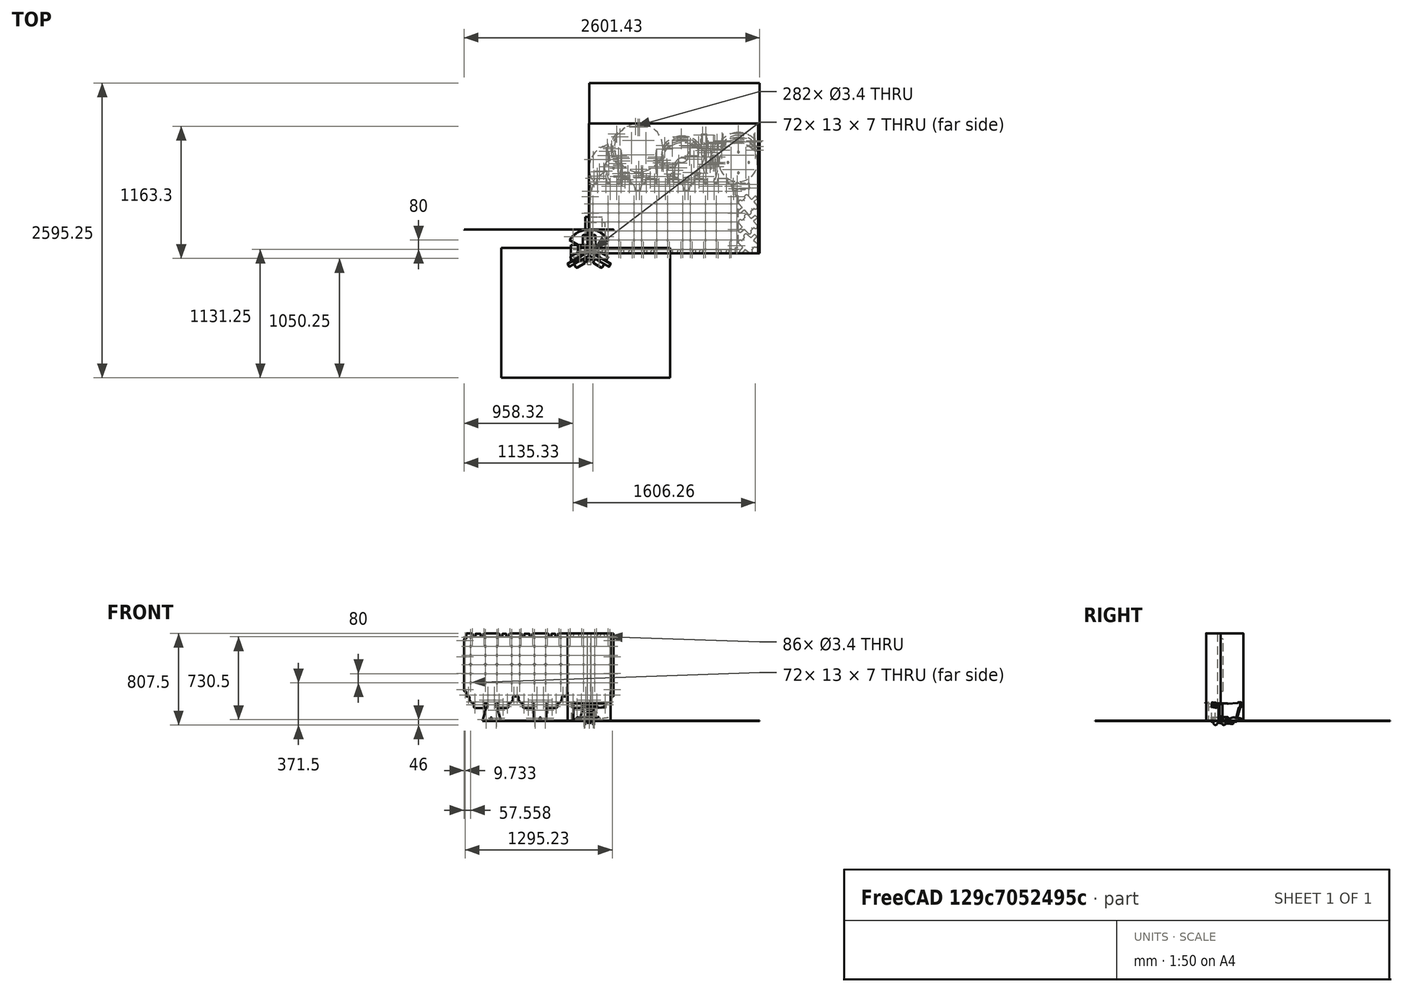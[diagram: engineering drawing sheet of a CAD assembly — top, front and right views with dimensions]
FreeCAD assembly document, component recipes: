
FREECAD ASSEMBLY — COMPONENT RECIPES ("composit_stand_small_3")

This assembly document has 19 components, labeled P0..P18 below (a component is one placed body or linked part). 18 of them carry a construction recipe — the FreeCAD feature program that regenerates the part from scratch, quoted from this document or its linked companion documents; the rest are supplied as boundary geometry only. No exploded tour is included for this assembly.
NOTE — this tour is split across 2 documents so each fits a 32k-token context. This is document 1: the component sections continue in the remaining 1 document, each repeating the header above.
COMPONENT P0 — recipe-attached ("gutter001_material_0.50ansi", modeled in this document).
Construction recipe (the document's own serialized feature program — sketch geometry with constraints, then the solid features built on it; lengths are millimeters unless a unit is written):

FEATURE [Sketcher::SketchObject] Sketch  label="gutter_side_sketch"
  FullyConstrained = true
  MapMode = 5
  Support = -> [XY_Plane]
  expr: .AttachmentOffset.Base.x = 0
  expr: .Constraints.little_distance = <<gutter>>.low_edge_length + (<<main>>.inner_width - <<main>>.thickness * 2) / 2 - 3mm
  expr: Constraints[12] = <<gutter>>.length
  expr: Constraints[27] = <<gutter>>.bend_angle + 90°
  sketch-geometry (15):
    g0: LineSegment StartX=0 StartY=150 StartZ=0 EndX=13.5 EndY=150 EndZ=0
    g1: LineSegment StartX=27 StartY=0 StartZ=0 EndX=0 EndY=0 EndZ=0
    g2: LineSegment StartX=15 StartY=148.5 StartZ=0 EndX=15 EndY=120 EndZ=0
    g3: LineSegment StartX=15 StartY=120 StartZ=0 EndX=31.2589 EndY=120 EndZ=0
    g4: GeomPoint X=27 Y=150 Z=0
    g5: ArcOfCircle CenterX=31.2589 CenterY=116.5 CenterZ=0 NormalX=0 NormalY=0 NormalZ=1 AngleXU=0 Radius=3.5 StartAngle=6.21662 EndAngle=7.85398
    g6: GeomPoint X=27 Y=0 Z=0
    g7: ArcOfCircle CenterX=13.5 CenterY=148.5 CenterZ=0 NormalX=0 NormalY=0 NormalZ=1 AngleXU=0 Radius=1.5 StartAngle=-3.6e-15 EndAngle=1.5708
    g8: GeomPoint X=15 Y=150 Z=0
    g9: LineSegment StartX=34.7511 StartY=116.267 StartZ=0 EndX=27.4178 EndY=6.26718 EndZ=0
    g10: LineSegment StartX=27.4178 StartY=6.26718 StartZ=0 EndX=27 EndY=0 EndZ=0
    g11: ArcOfCircle CenterX=23.9256 CenterY=6.5 CenterZ=0 NormalX=0 NormalY=0 NormalZ=1 AngleXU=0 Radius=3.5 StartAngle=4.71239 EndAngle=6.21662
    g12: LineSegment StartX=0 StartY=0 StartZ=0 EndX=0 EndY=3 EndZ=0
    g13: LineSegment StartX=0 StartY=3 StartZ=0 EndX=0 EndY=150 EndZ=0
    g14: LineSegment StartX=0 StartY=3 StartZ=0 EndX=23.9256 EndY=3 EndZ=0
  constraints (36):
    c: Coincident(g-1,g12)
    c: PointOnObject(g13,g-2)
    c: Coincident(g13,g0)
    c: Horizontal(g0)
    c: PointOnObject(g6,g-1)
    c: Coincident(g1,g12)
    c: Distance(g1,g6) = 27  'little_distance'
    c: Vertical(g2)
    c: Coincident(g3,g2)
    c: Horizontal(g3)
    c: DistanceY(g2,g8) = 30
    c: PointOnObject(g4,g0)
    c: Distance(g6,g4) = 150
    c: Distance(g0,g8) = 15
    c: Tangent(g3,g5) = 1.5708
    c: Diameter(g5) = 7
    c: PointOnObject(g8,g0)
    c: PointOnObject(g8,g2)
    c: Tangent(g0,g7) = 1.5708
    c: Tangent(g2,g7) = 1.5708
    c: Diameter(g7) = 3
    c: Tangent(g9,g5) = 1.5708
    c: Vertical(g4,g6)
    c: Coincident(g1,g6)
    c: Coincident(g10,g1)
    c: Coincident(g9,g10)
    c: Parallel(g9,g10)
    c: Angle(g10,g-1) = 1.63736
    c: Coincident(g12,g13)
    c: Vertical(g12)
    c: Coincident(g14,g12)
    c: Horizontal(g14)
    c: Tangent(g11,g9) = 1.5708
    c: Tangent(g14,g11) = -1.5708
    c: Equal(g11,g5)
    c: DistanceY(g12,g12) = 3
FEATURE [PartDesign::Pad] Pad  label="gutter_side_pad"
  Direction = (0,0,1)
  Length = 0.3
  Length2 = 10
  Profile = -> Sketch
  ReferenceAxis = -> Sketch [N_Axis]
  Type = 0
FEATURE [Sketcher::SketchObject] Sketch010
  FullyConstrained = true
  MapMode = 5
  Support = -> [XY_Plane]
  expr: Constraints[2] = -(<<main>>.inner_width / 2 - <<main>>.thickness - <<main>>.bend_r)
  expr: Constraints[3] = <<gutter>>.length
  sketch-geometry (1):
    g0: LineSegment StartX=-9.99 StartY=0 StartZ=0 EndX=-9.99 EndY=150 EndZ=0
  constraints (4):
    c: PointOnObject(g0,g-1)
    c: Vertical(g0)
    c: DistanceX(g0) = -9.99
    c: DistanceY(g0) = 150
FEATURE [PartDesign::Mirrored] Mirrored005
  BaseFeature = -> Pad
  MirrorPlane = -> YZ_Plane
  Originals = -> [Pad]
  Refine = true
FEATURE [PartDesign::CoordinateSystem] Local_CS001
  AttacherType = Attacher::AttachEngine3D
  AttachmentOffset = pos=(-30,0,0) rot=(0,0,1;0.066568rad)
  MapMode = 5
  Placement = pos=(-30,0,0) rot=(0,0,1;0.066568rad)
  Support = -> [XY_Plane]
  expr: .AttachmentOffset.Base.x = -(<<gutter>>.low_edge_length + (<<main>>.inner_width - <<main>>.thickness * 2) / 2)
  expr: .AttachmentOffset.Rotation.Angle = <<gutter>>.bend_angle
  expr: .AttachmentOffset.Rotation.Yaw = <<gutter>>.bend_angle
FEATURE [PartDesign::CoordinateSystem] Local_CS002
  AttacherType = Attacher::AttachEngine3D
  AttachmentOffset = pos=(30,0,0) rot=(0,0,1;-0.066568rad)
  MapMode = 5
  Placement = pos=(30,0,0) rot=(0,0,1;6.21662rad)
  Support = -> [XY_Plane]
  expr: .AttachmentOffset.Base.x = <<gutter>>.low_edge_length + (<<main>>.inner_width - <<main>>.thickness * 2) / 2
  expr: .AttachmentOffset.Rotation.Angle = -<<gutter>>.bend_angle
FEATURE [PartDesign::CoordinateSystem] Local_CS003
  AttacherType = Attacher::AttachEngine3D
  AttachmentOffset = pos=(0,60,0) rot=(0,0,1;1.5708rad)
  MapMode = 5
  Placement = pos=(33.9911,59.8671,0) rot=(0,0,1;1.50423rad)
  Support = -> [Local_CS002]
  expr: .AttachmentOffset.Base.y = <<gutter>>.plane_middle
FEATURE [PartDesign::CoordinateSystem] Local_CS004
  AttacherType = Attacher::AttachEngine3D
  AttachmentOffset = pos=(2,60,0) rot=(0,0,1;-1.5708rad)
  MapMode = 5
  Placement = pos=(-31.9956,60.0001,0) rot=(0,0,1;4.77896rad)
  Support = -> [Local_CS001]
  expr: .AttachmentOffset.Base.y = <<gutter>>.plane_middle
FEATURE [PartDesign::Plane] DatumPlane003
  Length = 91.4351
  MapMode = 4
  Placement = pos=(33.9911,59.8671,0) rot=(0.023538,0.706911,0.706911;3.09453rad)
  ResizeMode = 0
  Support = -> [Local_CS003]
  Width = 62.5599
FEATURE [PartDesign::Plane] DatumPlane004
  Length = 91.4351
  MapMode = 4
  Placement = pos=(-31.9956,60.0001,0) rot=(0.998893,0.03326,0.03326;1.5719rad)
  ResizeMode = 0
  Support = -> [Local_CS004]
  Width = 62.5599
FEATURE [PartDesign::Plane] DatumPlane005
  AttachmentOffset = pos=(0,-1,0) rot=(0,0,1;0rad)
  Length = 202.865
  MapMode = 5
  Placement = pos=(34.9889,59.8006,0) rot=(0,0,1;1.50423rad)
  ResizeMode = 0
  Support = -> [Local_CS003]
  Width = 102.646
FEATURE [PartDesign::Plane] DatumPlane006
  Length = 202.865
  MapMode = 5
  Placement = pos=(-31.9956,60.0001,0) rot=(0,0,-1;1.50423rad)
  ResizeMode = 0
  Support = -> [Local_CS004]
  Width = 102.646
FEATURE [Sketcher::SketchObject] Sketch037
  AttachmentOffset = pos=(30,2,0) rot=(0,0,1;0rad)
  FullyConstrained = true
  MapMode = 5
  Placement = pos=(33.9911,89.9337,0) rot=(0,0,1;1.50423rad)
  Support = -> [Local_CS003]
  expr: .AttachmentOffset.Base.x = <<dropper>>.distance_between_droppers1 / 2
  expr: Constraints[10] = <<dropper>>.d
  sketch-geometry (8):
    g0: LineSegment StartX=0 StartY=11.625 StartZ=0 EndX=1 EndY=11.625 EndZ=0
    g1: ArcOfCircle CenterX=1 CenterY=0 CenterZ=0 NormalX=0 NormalY=0 NormalZ=1 AngleXU=0 Radius=11.625 StartAngle=0.450911 EndAngle=1.5708
    g2: ArcOfCircle CenterX=17.127 CenterY=0 CenterZ=0 NormalX=0 NormalY=0 NormalZ=1 AngleXU=0 Radius=3 StartAngle=0.25268 EndAngle=1.29556
    g3: LineSegment StartX=12.0914 StartY=4.53943 StartZ=0 EndX=17.9423 EndY=2.88708 EndZ=0
    g4: LineSegment StartX=0 StartY=11.625 StartZ=0 EndX=0 EndY=0 EndZ=0
    g5: LineSegment StartX=0 StartY=0 StartZ=0 EndX=21 EndY=0 EndZ=0
    g6: ArcOfCircle CenterX=21 CenterY=1 CenterZ=0 NormalX=0 NormalY=0 NormalZ=1 AngleXU=0 Radius=1 StartAngle=3.39427 EndAngle=4.71239
    g7: ArcOfCircle CenterX=12.3631 CenterY=5.5018 CenterZ=0 NormalX=0 NormalY=0 NormalZ=1 AngleXU=0 Radius=1 StartAngle=3.5925 EndAngle=4.43715
  constraints (22):
    c: PointOnObject(g0,g-2)
    c: Horizontal(g0)
    c: PointOnObject(g2,g-1)
    c: Tangent(g3,g2) = 1.5708
    c: Tangent(g1,g0) = 1.5708
    c: Coincident(g4,g0)
    c: Coincident(g4,g-1)
    c: Coincident(g5,g4)
    c: Diameter(g2) = 6
    c: Angle(g3,g-1) = 0.275238
    c: Diameter(g1) = 23.25
    c: PointOnObject(g1,g-1)
    c: Distance(g0) = 1
    c: Horizontal(g5)
    c: Tangent(g6,g5) = -1.5708
    c: Tangent(g6,g2) = 1.5708
    c: Diameter(g6) = 2
    c: Distance(g5) = 21
    c: Tangent(g3,g7) = -1.5708
    c: Tangent(g1,g7) = 1.5708
    c: Diameter(g7) = 2
    c: DistanceY(g2) = 2.88708  'arc_height'
FEATURE [PartDesign::Pocket] Pocket008
  BaseFeature = -> Mirrored005
  Direction = (0,0,-1)
  Length = 5
  Length2 = 5
  Midplane = true
  Profile = -> Sketch037
  ReferenceAxis = -> Sketch037 [N_Axis]
  Type = 1
FEATURE [PartDesign::Mirrored] Mirrored006
  MirrorPlane = -> Sketch037 [V_Axis]
FEATURE [PartDesign::Mirrored] Mirrored007
  MirrorPlane = -> DatumPlane003
FEATURE [PartDesign::MultiTransform] MultiTransform002
  BaseFeature = -> Pocket008
  Originals = -> [Pocket008]
  Transformations = -> [Mirrored006,Mirrored007]
FEATURE [PartDesign::SubShapeBinder] Binder
  AttacherType = Attacher::AttachEngine3D
  AttachmentOffset = pos=(35,0,0) rot=(0,0,1;0rad)
  BindCopyOnChange = 0
  BindMode = 0
  ClaimChildren = true
  Context = -> Body [Binder.]
  Fuse = false
  MakeFace = true
  MapMode = 5
  OffsetFill = false
  OffsetIntersection = false
  OffsetJoinType = 0
  OffsetOpenResult = false
  PartialLoad = false
  Placement = pos=(-28.1674,25.0777,0) rot=(0,0,-1;1.50423rad)
  Relative = false
  _Version = 2
  expr: .AttachmentOffset.Base.x = <<dropper>>.distance_between_droppers2 / 2
FEATURE [PartDesign::Pocket] Pocket009
  BaseFeature = -> MultiTransform002
  Direction = (0,0,-1)
  Length = 5
  Length2 = 5
  Midplane = true
  Profile = -> Binder
  Type = 1
FEATURE [PartDesign::Plane] DatumPlane007
  Length = 91.4351
  MapMode = 4
  Placement = pos=(-28.1674,25.0777,0) rot=(0.998893,0.03326,0.03326;1.5719rad)
  ResizeMode = 0
  Support = -> [Binder]
  Width = 62.5599
FEATURE [PartDesign::Mirrored] Mirrored008
  MirrorPlane = -> DatumPlane007
FEATURE [PartDesign::Mirrored] Mirrored009
  MirrorPlane = -> DatumPlane004
FEATURE [PartDesign::MultiTransform] MultiTransform003
  BaseFeature = -> Pocket009
  Originals = -> [Pocket009]
  Transformations = -> [Mirrored008,Mirrored009]
FEATURE [Sketcher::SketchObject] Sketch038
  FullyConstrained = true
  MapMode = 5
  Support = -> [XY_Plane]
  expr: Constraints[2] = <<main>>.inner_width / 2 - <<main>>.thickness - <<main>>.bend_r
  expr: Constraints[3] = <<gutter>>.length
  sketch-geometry (1):
    g0: LineSegment StartX=9.99 StartY=0 StartZ=0 EndX=9.99 EndY=150 EndZ=0
  constraints (4):
    c: PointOnObject(g0,g-1)
    c: Vertical(g0)
    c: DistanceX(g0) = 9.99
    c: DistanceY(g0) = 150
FEATURE [Sketcher::SketchObject] Sketch039
  AttachmentOffset = pos=(51,14,0) rot=(0,0,1;0rad)
  FullyConstrained = true
  MapMode = 5
  Placement = pos=(24.4124,111.619,0) rot=(0,0,1;1.50423rad)
  Support = -> [DatumPlane005]
  expr: .AttachmentOffset.Base.x = <<main>>.gutter_fix_holes_distance
  expr: Constraints[1] = <<main>>.rivet_d
  sketch-geometry (1):
    g0: Circle CenterX=0 CenterY=0 CenterZ=0 NormalX=0 NormalY=0 NormalZ=1 AngleXU=0 Radius=1.7
  constraints (2):
    c: Coincident(g0,g-1)
    c: Diameter(g0) = 3.4
FEATURE [PartDesign::Pocket] Pocket010
  BaseFeature = -> MultiTransform003
  Direction = (0,0,-1)
  Length = 5
  Length2 = 5
  Midplane = true
  Profile = -> Sketch039
  ReferenceAxis = -> Sketch039 [N_Axis]
  Type = 1
FEATURE [PartDesign::Mirrored] Mirrored010
  MirrorPlane = -> DatumPlane003
FEATURE [PartDesign::Mirrored] Mirrored011
  MirrorPlane = -> YZ_Plane
FEATURE [PartDesign::MultiTransform] MultiTransform004
  BaseFeature = -> Pocket010
  Originals = -> [Pocket010]
  Transformations = -> [Mirrored010,Mirrored011]
FEATURE [PartDesign::FeaturePython] Fold  # WARN: FeaturePython — macro-defined, semantics opaque (R4)
  BaseFeature = -> MultiTransform004
  BendLine = -> Sketch038
  Position = 0
  angle = 90
  baseObject = -> MultiTransform004 [Face4]
  invert = false
  invertbend = true
  kfactor = 0.01
  radius = 0.01
  unfold = false
  expr: radius = <<main>>.bend_r
FEATURE [PartDesign::FeaturePython] Fold002  # WARN: FeaturePython — macro-defined, semantics opaque (R4)
  BaseFeature = -> Fold
  BendLine = -> Sketch010
  Position = 0
  angle = 90
  baseObject = -> Fold [Face2]
  invert = false
  invertbend = false
  kfactor = 0.01
  radius = 0.01
  unfold = false
  expr: radius = <<main>>.bend_r
FEATURE [PartDesign::CoordinateSystem] Local_CS024
  AttacherType = Attacher::AttachEngine3D
  AttachmentOffset = pos=(0,60,-10.3215) rot=(-1,0,0;0.066568rad)
  MapMode = 5
  Placement = pos=(0,60,-10.3215) rot=(-1,0,0;0.066568rad)
  Support = -> [XY_Plane]
  expr: .AttachmentOffset.Base.y = <<gutter>>.plane_middle
  expr: .AttachmentOffset.Base.z = (-6.929mm - 13.714mm) / 2
  expr: .AttachmentOffset.Rotation.Roll = -<<gutter>>.bend_angle
FEATURE [Sketcher::SketchObject] Sketch115
  FullyConstrained = true
  MapMode = 5
  Support = -> [XY_Plane]
  expr: Constraints[1] = <<main>>.rivet_d
  sketch-geometry (1):
    g0: Circle CenterX=0 CenterY=145 CenterZ=0 NormalX=0 NormalY=0 NormalZ=1 AngleXU=0 Radius=1.7
  constraints (3):
    c: PointOnObject(g0,g-2)
    c: Diameter(g0) = 3.4
    c: DistanceY(g0) = 145
FEATURE [PartDesign::Pocket] Pocket070
  BaseFeature = -> Fold002
  Direction = (0,0,-1)
  Length = 5
  Length2 = 5
  Midplane = true
  Profile = -> Sketch115
  ReferenceAxis = -> Sketch115 [N_Axis]
  Type = 1
FEATURE [PartDesign::Body] Body  label="gutter001_material_0.50ansi"
  Group = -> [Sketch,Pad,Mirrored005,Local_CS001,Local_CS002,Local_CS003,Local_CS004,DatumPlane003,DatumPlane004,DatumPlane005,DatumPlane006,Sketch037,Pocket008,MultiTransform002,Mirrored006,Mirrored007,Binder,Pocket009,MultiTransform003,Mirrored008,DatumPlane007,Mirrored009,Sketch010,Sketch038,Sketch039,Pocket010,MultiTransform004,Mirrored010,Mirrored011,Fold,Fold002,Local_CS024,Sketch115,Pocket070]
  Origin = -> Origin
  Tip = -> Pocket070
COMPONENT P1 — recipe-attached ("Body001_material_0.30ansi", modeled in this document).
Construction recipe (the document's own serialized feature program — sketch geometry with constraints, then the solid features built on it; lengths are millimeters unless a unit is written):

FEATURE [Sketcher::SketchObject] Sketch003  label="main_sketch"
  FullyConstrained = true
  MapMode = 5
  Support = -> [XY_Plane001]
  expr: Constraints[30] = <<main>>.end_face_width
  expr: Constraints[31] = <<main>>.work_plane_width
  expr: Constraints[44] = <<main>>.al_thickness
  sketch-geometry (17):
    g0: LineSegment StartX=-16 StartY=9.2376 StartZ=0 EndX=-16 EndY=209.238 EndZ=0
    g1: LineSegment StartX=-16 StartY=209.238 StartZ=0 EndX=16 EndY=209.238 EndZ=0
    g2: LineSegment StartX=16 StartY=209.238 StartZ=0 EndX=16 EndY=9.2376 EndZ=0
    g3: LineSegment StartX=16 StartY=9.2376 StartZ=0 EndX=189.205 EndY=-90.7624 EndZ=0
    g4: LineSegment StartX=189.205 StartY=-90.7624 StartZ=0 EndX=173.205 EndY=-118.475 EndZ=0
    g5: LineSegment StartX=173.205 StartY=-118.475 StartZ=0 EndX=0 EndY=-18.4752 EndZ=0
    g6: LineSegment StartX=0 StartY=-18.4752 StartZ=0 EndX=-173.205 EndY=-118.475 EndZ=0
    g7: LineSegment StartX=-173.205 StartY=-118.475 StartZ=0 EndX=-189.205 EndY=-90.7624 EndZ=0
    g8: LineSegment StartX=-189.205 StartY=-90.7624 StartZ=0 EndX=-16 EndY=9.2376 EndZ=0
    g9: LineSegment StartX=-16 StartY=9.2376 StartZ=0 EndX=0 EndY=0 EndZ=0
    g10: LineSegment StartX=0 StartY=0 StartZ=0 EndX=16 EndY=9.2376 EndZ=0
    g11: LineSegment StartX=0 StartY=0 StartZ=0 EndX=0 EndY=-18.4752 EndZ=0
    g12: LineSegment StartX=189.205 StartY=-90.7624 StartZ=0 EndX=13 EndY=10.9697 EndZ=0
    g13: LineSegment StartX=16 StartY=209.238 StartZ=0 EndX=16 EndY=9.42236 EndZ=0
    g14: LineSegment StartX=16 StartY=9.42236 StartZ=0 EndX=15.7 EndY=9.42236 EndZ=0
    g15: LineSegment StartX=13 StartY=10.9697 StartZ=0 EndX=13 EndY=30.9697 EndZ=0
    g16: LineSegment StartX=13 StartY=10.9697 StartZ=0 EndX=6.66667 EndY=0 EndZ=0
  constraints (56):
    c: Vertical(g0)
    c: Coincident(g0,g1)
    c: Horizontal(g1)
    c: Coincident(g1,g2)
    c: Vertical(g2)
    c: Coincident(g2,g3)
    c: Coincident(g3,g4)
    c: Coincident(g4,g5)
    c: PointOnObject(g5,g-2)
    c: Coincident(g5,g6)
    c: Coincident(g6,g7)
    c: Coincident(g8,g7)
    c: Equal(g2,g6)
    c: Equal(g6,g5)
    c: Equal(g5,g3)
    c: Equal(g4,g7)
    c: Equal(g7,g1)
    c: Perpendicular(g4,g5)
    c: Perpendicular(g4,g3)
    c: Perpendicular(g7,g6)
    c: Perpendicular(g8,g7)
    c: Angle(g6,g5) = 2.0944
    c: Angle(g3,g2) = 2.0944
    c: Coincident(g9,g0)
    c: Coincident(g9,g-1)
    c: Coincident(g10,g9)
    c: Coincident(g10,g2)
    c: Coincident(g11,g9)
    c: Coincident(g11,g5)
    c: Equal(g10,g11)
    c: DistanceX(g1,g1) = 32
    c: DistanceY(g2,g2) = 200
    c: DistanceY(g9,g2) = 9.2376  'petal_offset'
    c: DistanceY(g0) = 9.2376  'petal_conn_y'
    c: Coincident(g8,g0)
    c: DistanceX(g2) = 16  'petal_conn_x'
    c: Distance(g9,g1) = 209.848  'max_r'
    c: Distance(g10) = 18.4752  'planes_intersec_r'
    c: DistanceY(g9,g1) = 209.238  'total_petal_length'
    c: Coincident(g12,g4)
    c: Coincident(g13,g1)
    c: PointOnObject(g13,g2)
    c: Coincident(g14,g13)
    c: Horizontal(g14)
    c: DistanceX(g14,g14) = 0.3
    c: Distance(g14,g12) = 0.01
    c: PointOnObject(g2,g12)
    c: Distance(g12,g13) = 3
    c: Coincident(g15,g12)
    c: Vertical(g15)
    c: DistanceY(g15,g15) = 20
    c: DistanceY(g15) = 30.9697  'overlap_end_y'
    c: Coincident(g16,g12)
    c: Perpendicular(g16,g12)
    c: Distance(g9,g16) = 5.7735  'overlap_bend_offset'
    c: PointOnObject(g16,g-1)
FEATURE [PartDesign::FeaturePython] BaseBend001  # WARN: FeaturePython — macro-defined, semantics opaque (R4)
  BendSide = 0
  BendSketch = -> Sketch003
  MidPlane = false
  Reverse = false
  length = 774
  radius = 0.01
  thickness = 0.3
  expr: length = <<main>>.total_length
  expr: radius = <<main>>.bend_r
FEATURE [PartDesign::CoordinateSystem] Local_CS
  AttacherType = Attacher::AttachEngine3D
  AttachmentOffset = pos=(0,9.2376,0) rot=(0,0,1;0rad)
  MapMode = 5
  Placement = pos=(0,9.2376,0) rot=(0,0,1;0rad)
  Support = -> [XY_Plane001]
  expr: .AttachmentOffset.Base.y = Sketch003.Constraints.petal_offset
FEATURE [PartDesign::CoordinateSystem] Local_CS011
  AttacherType = Attacher::AttachEngine3D
  AttachmentOffset = pos=(0,100,0) rot=(0,0,1;0rad)
  MapMode = 5
  Placement = pos=(0,109.238,0) rot=(0,0,1;0rad)
  Support = -> [Local_CS]
  expr: .AttachmentOffset.Base.y = <<main>>.work_plane_width / 2
FEATURE [PartDesign::Plane] DatumPlane011
  AttachmentOffset = pos=(0,0,0) rot=(0,0,1;0.523599rad)
  Length = 592.916
  MapMode = 5
  Placement = pos=(0,0,0) rot=(0,0,1;0.523599rad)
  ResizeMode = 0
  Support = -> [XY_Plane001]
  Width = 577.285
FEATURE [PartDesign::CoordinateSystem] Local_CS035
  AttacherType = Attacher::AttachEngine3D
  AttachmentOffset = pos=(0,0,774) rot=(0,0,1;0rad)
  MapMode = 5
  Placement = pos=(0,109.238,774) rot=(0,0,1;0rad)
  Support = -> [Local_CS011]
  expr: .AttachmentOffset.Base.z = <<main>>.total_length
FEATURE [PartDesign::CoordinateSystem] Local_CS036  label="droppers_center"
  AttacherType = Attacher::AttachEngine3D
  AttachmentOffset = pos=(0,0,-19) rot=(0,0,1;0rad)
  MapMode = 5
  Placement = pos=(0,109.238,755) rot=(0,0,1;0rad)
  Support = -> [Local_CS035]
FEATURE [PartDesign::CoordinateSystem] Local_CS037  label="gutter_fixture_center"
  AttacherType = Attacher::AttachEngine3D
  AttachmentOffset = pos=(0,0,-12) rot=(0,0,1;0rad)
  MapMode = 5
  Placement = pos=(0,109.238,743) rot=(0,0,1;0rad)
  Support = -> [Local_CS036]
FEATURE [PartDesign::CoordinateSystem] Local_CS038  label="modules_top_center"
  AttacherType = Attacher::AttachEngine3D
  AttachmentOffset = pos=(0,0,-5) rot=(0,0,1;0rad)
  MapMode = 5
  Placement = pos=(0,109.238,738) rot=(0,0,1;0rad)
  Support = -> [Local_CS037]
FEATURE [Sketcher::SketchObject] Sketch112
  FullyConstrained = true
  MapMode = 5
  Placement = pos=(0,0,0) rot=(0.57735,0.57735,0.57735;2.0944rad)
  Support = -> [YZ_Plane001]
  expr: Constraints[10] = <<module>>.module_hole_x
  expr: Constraints[11] = <<module>>.module_hole_y
  sketch-geometry (5):
    g0: LineSegment StartX=-6.5 StartY=-3.5 StartZ=0 EndX=-6.5 EndY=3.5 EndZ=0
    g1: LineSegment StartX=-6.5 StartY=3.5 StartZ=0 EndX=6.5 EndY=3.5 EndZ=0
    g2: LineSegment StartX=6.5 StartY=3.5 StartZ=0 EndX=6.5 EndY=-3.5 EndZ=0
    g3: LineSegment StartX=6.5 StartY=-3.5 StartZ=0 EndX=-6.5 EndY=-3.5 EndZ=0
    g4: GeomPoint X=0 Y=0 Z=0
  constraints (12):
    c: Coincident(g0,g1)
    c: Coincident(g1,g2)
    c: Coincident(g2,g3)
    c: Coincident(g3,g0)
    c: Horizontal(g1)
    c: Horizontal(g3)
    c: Vertical(g0)
    c: Vertical(g2)
    c: Symmetric(g1,g0,g4)
    c: Coincident(g4,g-1)
    c: DistanceX(g1,g1) = 13
    c: DistanceY(g2,g2) = 7
FEATURE [Sketcher::SketchObject] Sketch113
  FullyConstrained = true
  MapMode = 5
  Placement = pos=(0,0,0) rot=(0.57735,0.57735,0.57735;2.0944rad)
  Support = -> [YZ_Plane001]
  expr: Constraints[18] = <<dropper>>.d + 2mm
  expr: Constraints[19] = <<dropper>>.center_height_offset
  sketch-geometry (8):
    g0: ArcOfCircle CenterX=0 CenterY=0 CenterZ=0 NormalX=0 NormalY=0 NormalZ=1 AngleXU=0 Radius=12.625 StartAngle=3.14159 EndAngle=6.28319
    g1: LineSegment StartX=12.625 StartY=-3.1e-15 StartZ=0 EndX=12.625 EndY=12.5 EndZ=0
    g2: LineSegment StartX=-12.625 StartY=1.5e-15 StartZ=0 EndX=-12.625 EndY=12.5 EndZ=0
    g3: ArcOfCircle CenterX=15.125 CenterY=12.5 CenterZ=0 NormalX=0 NormalY=0 NormalZ=1 AngleXU=0 Radius=2.5 StartAngle=1.5708 EndAngle=3.14159
    g4: ArcOfCircle CenterX=-15.125 CenterY=12.5 CenterZ=0 NormalX=0 NormalY=0 NormalZ=1 AngleXU=0 Radius=2.5 StartAngle=0 EndAngle=1.5708
    g5: LineSegment StartX=-15.125 StartY=15 StartZ=0 EndX=-15.125 EndY=19 EndZ=0
    g6: LineSegment StartX=-15.125 StartY=19 StartZ=0 EndX=15.125 EndY=19 EndZ=0
    g7: LineSegment StartX=15.125 StartY=19 StartZ=0 EndX=15.125 EndY=15 EndZ=0
  constraints (24):
    c: Coincident(g0,g-1)
    c: PointOnObject(g0,g-1)
    c: PointOnObject(g0,g-1)
    c: Coincident(g1,g0)
    c: Vertical(g1)
    c: Coincident(g2,g0)
    c: Vertical(g2)
    c: Coincident(g5,g4)
    c: Vertical(g5)
    c: Coincident(g6,g5)
    c: Horizontal(g6)
    c: Coincident(g7,g6)
    c: Coincident(g7,g3)
    c: Vertical(g7)
    c: Perpendicular(g3,g7)
    c: Tangent(g3,g1) = 1.5708
    c: Tangent(g4,g2) = -1.5708
    c: Perpendicular(g4,g5)
    c: Diameter(g0) = 25.25
    c: Distance(g0,g6) = 19
    c: Equal(g4,g3)
    c: Diameter(g4) = 5
    c: DistanceY(g7,g7) = 4
    c: Equal(g5,g7)
FEATURE [Sketcher::SketchObject] Sketch128
  FullyConstrained = true
  MapMode = 5
  Placement = pos=(0,0,0) rot=(0.57735,0.57735,0.57735;2.0944rad)
  Support = -> [YZ_Plane001]
  expr: Constraints[11] = Spreadsheet001.cover_plane_bend
  expr: Constraints[5] = <<main>>.basin_height
  sketch-geometry (5):
    g0: LineSegment StartX=73 StartY=116.654 StartZ=0 EndX=165.646 EndY=124.76 EndZ=0
    g1: LineSegment StartX=165.646 StartY=124.76 StartZ=0 EndX=162.116 EndY=165.105 EndZ=0
    g2: LineSegment StartX=162.116 StartY=165.105 StartZ=0 EndX=69.4702 EndY=157 EndZ=0
    g3: LineSegment StartX=69.4702 StartY=157 StartZ=0 EndX=73 EndY=116.654 EndZ=0
    g4: GeomPoint X=115.793 Y=161.053 Z=0
  constraints (15):
    c: Coincident(g0,g1)
    c: Coincident(g1,g2)
    c: Coincident(g2,g3)
    c: Coincident(g3,g0)
    c: DistanceX(g0) = 73  'offset_x'
    c: DistanceY(g2) = 157
    c: Distance(g3) = 40.5  'height'
    c: Distance(g0) = 93  'length'
    c: Parallel(g1,g3)
    c: Parallel(g0,g2)
    c: Perpendicular(g0,g3)
    c: Angle(g-1,g0) = 0.0872665
    c: Symmetric(g2,g1,g4)
    c: DistanceX(g4) = 115.793  'top_center_x'
    c: DistanceY(g4) = 161.053  'top_center_y'
FEATURE [PartDesign::Pocket] Pocket081
  BaseFeature = -> BaseBend001
  Direction = (-1,2e-16,-3e-16)
  Length = 5
  Length2 = 5
  Midplane = true
  Profile = -> Sketch128
  ReferenceAxis = -> Sketch128 [N_Axis]
  Type = 1
FEATURE [PartDesign::PolarPattern] PolarPattern016
  Angle = 360
  Axis = -> Z_Axis001
  BaseFeature = -> Pocket081
  Occurrences = 3
  Originals = -> [Pocket081]
FEATURE [PartDesign::FeaturePython] Bend  # WARN: FeaturePython — macro-defined, semantics opaque (R4)
  AutoMiter = true
  BaseFeature = -> PolarPattern016
  BendType = 0
  LengthList = [40]
  LengthSpec = 2
  ReliefFactor = 0.7
  UseReliefFactor = false
  angle = 85
  baseObject = -> PolarPattern016 [Edge67,Edge25,Edge211,Edge168,Edge96,Edge140]
  bendAList = [85]
  extend1 = 0
  extend2 = 0
  gap1 = 0.1
  gap2 = 0.1
  invert = false
  kfactor = 0.5
  length = 40
  maxExtendDist = 5
  minGap = 0.1
  minReliefGap = 1
  miterangle1 = 0
  miterangle2 = 0
  offset = 0
  radius = 0.1
  reliefType = 0
  reliefd = 1
  reliefw = 0.8
  sketchflip = false
  sketchinvert = false
  unfold = false
  expr: angle = 90deg - <<main>>.cover_bend_mid
FEATURE [PartDesign::Pocket] Pocket007
  BaseFeature = -> Bend
  Direction = (-1,2e-16,-3e-16)
  Length = 13.01
  Length2 = 5
  Profile = -> Sketch012
  ReferenceAxis = -> Sketch012 [N_Axis]
  Reversed = true
  Type = 0
  expr: Length = <<main>>.end_face_width / 2 - <<main>>.thickness + <<main>>.bend_r
FEATURE [Sketcher::SketchObject] Sketch129
  AttachmentOffset = pos=(0,0,0) rot=(0,1,0;3.66519rad)
  FullyConstrained = true
  MapMode = 5
  Placement = pos=(0,0,0) rot=(-0.186157,0.694747,0.694747;3.50969rad)
  Support = -> [XZ_Plane001]
  expr: .Constraints.height = Sketch128.Constraints.height
  expr: .Constraints.length = Sketch128.Constraints.length
  expr: Constraints[20] = <<main>>.cover_plane_bend
  expr: Constraints[24] = Sketch128.Constraints.top_center_x
  expr: Constraints[25] = Sketch128.Constraints.top_center_y
  expr: Constraints[8] = <<main>>.basin_height
  sketch-geometry (10):
    g0: LineSegment StartX=0 StartY=0 StartZ=0 EndX=168.826 EndY=0 EndZ=0
    g1: LineSegment StartX=168.826 StartY=0 StartZ=0 EndX=168.826 EndY=165.105 EndZ=0
    g2: LineSegment StartX=0 StartY=157 StartZ=0 EndX=0 EndY=0 EndZ=0
    g3: LineSegment StartX=73 StartY=116.654 StartZ=0 EndX=165.646 EndY=124.76 EndZ=0
    g4: LineSegment StartX=165.646 StartY=124.76 StartZ=0 EndX=162.116 EndY=165.105 EndZ=0
    g5: LineSegment StartX=162.116 StartY=165.105 StartZ=0 EndX=69.4702 EndY=157 EndZ=0
    g6: LineSegment StartX=69.4702 StartY=157 StartZ=0 EndX=73 EndY=116.654 EndZ=0
    g7: LineSegment StartX=168.826 StartY=165.105 StartZ=0 EndX=162.116 EndY=165.105 EndZ=0
    g8: LineSegment StartX=69.4702 StartY=157 StartZ=0 EndX=0 EndY=157 EndZ=0
    g9: GeomPoint X=115.793 Y=161.053 Z=0
  constraints (26):
    c: Coincident(g0,g1)
    c: Coincident(g1,g7)
    c: Coincident(g8,g2)
    c: Coincident(g2,g0)
    c: Horizontal(g0)
    c: Vertical(g1)
    c: Vertical(g2)
    c: Coincident(g0,g-1)
    c: DistanceY(g8) = 157
    c: Coincident(g3,g4)
    c: Coincident(g4,g5)
    c: Coincident(g5,g6)
    c: Coincident(g6,g3)
    c: Horizontal(g7)
    c: Coincident(g8,g5)
    c: Coincident(g7,g4)
    c: Perpendicular(g4,g3)
    c: Perpendicular(g5,g4)
    c: Perpendicular(g5,g6)
    c: Distance(g3,g1) = 3.18
    c: Angle(g-1,g5) = 0.0872665
    c: Distance(g6) = 40.5  'height'
    c: Distance(g3) = 93  'length'
    c: Symmetric(g6,g4,g9)
    c: DistanceX(g9) = 115.793
    c: DistanceY(g9) = 161.053
FEATURE [PartDesign::CoordinateSystem] Local_CS041
  AttacherType = Attacher::AttachEngine3D
  AttachmentOffset = pos=(115.793,161.053,16) rot=(0.029484,-0.675296,-0.736957;3.07726rad)
  MapMode = 5
  Placement = pos=(16,115.793,161.053) rot=(0,0.087156,-0.996195;1.5708rad)
  Support = -> [YZ_Plane001]
  expr: .AttachmentOffset.Base.x = Sketch128.Constraints.top_center_x
  expr: .AttachmentOffset.Base.y = Sketch128.Constraints.top_center_y
  expr: .AttachmentOffset.Base.z = <<main>>.end_face_width / 2
  expr: .AttachmentOffset.Rotation.Roll = 90° - <<main>>.cover_bend_mid
FEATURE [PartDesign::CoordinateSystem] Local_CS039
  AttacherType = Attacher::AttachEngine3D
  AttachmentOffset = pos=(0,-3,-3) rot=(0,1,0.71;0rad)
  MapMode = 5
  Placement = pos=(12.7499,116.031,158.336) rot=(0,0.087156,-0.996195;1.5708rad)
  Support = -> [Local_CS041]
  expr: .AttachmentOffset.Base.y = -<<main>>.thickness
  expr: .AttachmentOffset.Base.z = -<<main>>.thickness
FEATURE [Sketcher::SketchObject] Sketch130
  AttachmentOffset = pos=(0,40.5,0) rot=(0,0,1;0rad)
  FullyConstrained = true
  MapMode = 5
  Placement = pos=(56.3459,116.101,157.536) rot=(0,0.087156,-0.996195;1.5708rad)
  Support = -> [Local_CS041]
  expr: .AttachmentOffset.Base.y = Bend.length + 0.5mm
  expr: Constraints[14] = Sketch128.Constraints.length
  sketch-geometry (6):
    g0: ArcOfCircle CenterX=36.5 CenterY=-10 CenterZ=0 NormalX=0 NormalY=0 NormalZ=1 AngleXU=0 Radius=10 StartAngle=6.28318 EndAngle=7.85398
    g1: ArcOfCircle CenterX=-36.5 CenterY=-10 CenterZ=0 NormalX=0 NormalY=0 NormalZ=1 AngleXU=0 Radius=10 StartAngle=1.5708 EndAngle=3.14159
    g2: LineSegment StartX=-46.5 StartY=-10 StartZ=0 EndX=-46.5 EndY=0 EndZ=0
    g3: LineSegment StartX=-36.5 StartY=0 StartZ=0 EndX=-46.5 EndY=0 EndZ=0
    g4: LineSegment StartX=46.5 StartY=-10 StartZ=0 EndX=46.5 EndY=0 EndZ=0
    g5: LineSegment StartX=36.5 StartY=0 StartZ=0 EndX=46.5 EndY=0 EndZ=0
  constraints (17):
    c: PointOnObject(g0,g-1)
    c: PointOnObject(g1,g-1)
    c: Coincident(g2,g1)
    c: PointOnObject(g2,g-1)
    c: Vertical(g2)
    c: Tangent(g2,g1)
    c: Coincident(g3,g2)
    c: Coincident(g4,g0)
    c: PointOnObject(g4,g-1)
    c: Vertical(g4)
    c: Tangent(g4,g0)
    c: Coincident(g5,g4)
    c: Tangent(g5,g0) = 1.5708
    c: Tangent(g3,g1) = -1.5708
    c: DistanceX(g2,g4) = 93
    c: Symmetric(g1,g0,g-2)
    c: Diameter(g0) = 20
FEATURE [PartDesign::Mirrored] Mirrored040
  MirrorPlane = -> YZ_Plane001
FEATURE [PartDesign::PolarPattern] PolarPattern017
  Angle = 360
  Axis = -> Z_Axis001
  Occurrences = 3
FEATURE [PartDesign::CoordinateSystem] Local_CS042
  AttacherType = Attacher::AttachEngine3D
  AttachmentOffset = pos=(0,0,0) rot=(0,0,1;2.0944rad)
  MapMode = 5
  Placement = pos=(0,0,0) rot=(0,0,1;2.0944rad)
  Support = -> [XY_Plane001]
FEATURE [PartDesign::CoordinateSystem] Local_CS012
  AttacherType = Attacher::AttachEngine3D
  AttachmentOffset = pos=(16,115.793,161.053) rot=(0,0.087156,-0.996195;1.5708rad)
  MapMode = 5
  Placement = pos=(-108.28,-44.0402,161.053) rot=(-0.199622,0.115252,0.973071;0.541313rad)
  Support = -> [Local_CS042]
  expr: AttachmentOffset = Local_CS041.Placement
FEATURE [PartDesign::Plane] DatumPlane012
  Length = 674.323
  MapMode = 5
  Placement = pos=(-108.28,-44.0402,161.053) rot=(-0.199622,0.115252,0.973071;0.541313rad)
  ResizeMode = 0
  Support = -> [Local_CS012]
  Width = 659.7
FEATURE [PartDesign::Pocket] Pocket091
  BaseFeature = -> Pocket007
  Direction = (-0.5,-0.866025,-1e-16)
  Length = 16
  Length2 = 5
  Profile = -> Sketch134
  ReferenceAxis = -> Sketch134 [N_Axis]
  Refine = true
  Reversed = true
  Type = 0
  expr: Length = <<main>>.end_face_width / 2
FEATURE [Sketcher::SketchObject] Sketch136
  FullyConstrained = true
  MapMode = 5
  Support = -> [XY_Plane001]
  sketch-geometry (6):
    g0: LineSegment StartX=0 StartY=-100 StartZ=0 EndX=-86.6025 EndY=50 EndZ=0
    g1: LineSegment StartX=-86.6025 StartY=50 StartZ=0 EndX=86.6025 EndY=50 EndZ=0
    g2: LineSegment StartX=86.6025 StartY=50 StartZ=0 EndX=0 EndY=-100 EndZ=0
    g3: LineSegment StartX=-86.6025 StartY=50 StartZ=0 EndX=0 EndY=7.1e-15 EndZ=0
    g4: LineSegment StartX=0 StartY=7.1e-15 StartZ=0 EndX=86.6025 EndY=50 EndZ=0
    g5: LineSegment StartX=0 StartY=7.1e-15 StartZ=0 EndX=0 EndY=-100 EndZ=0
  constraints (15):
    c: PointOnObject(g0,g-2)
    c: Coincident(g1,g0)
    c: Horizontal(g1)
    c: Coincident(g2,g1)
    c: Coincident(g2,g0)
    c: Coincident(g3,g0)
    c: Coincident(g3,g-1)
    c: Coincident(g4,g3)
    c: Coincident(g4,g1)
    c: Coincident(g5,g3)
    c: Coincident(g5,g0)
    c: Equal(g3,g4)
    c: Equal(g4,g5)
    c: Equal(g0,g1)
    c: DistanceY(g1) = 50
FEATURE [PartDesign::Pocket] Pocket093
  BaseFeature = -> Pocket091
  Direction = (0,0,-1)
  Length = 157
  Length2 = 5
  Profile = -> Sketch136
  ReferenceAxis = -> Sketch136 [N_Axis]
  Reversed = true
  Type = 0
  expr: Length = <<main>>.basin_height
FEATURE [PartDesign::Pocket] Pocket083
  BaseFeature = -> Pocket093
  Direction = (-0.0871557,0.0868241,-0.992404)
  Length = 5
  Length2 = 5
  Midplane = true
  Profile = -> Sketch130
  ReferenceAxis = -> Sketch130 [N_Axis]
  Type = 1
FEATURE [PartDesign::MultiTransform] MultiTransform014
  BaseFeature = -> Pocket083
  Originals = -> [Pocket083]
  Transformations = -> [Mirrored040,PolarPattern017]
FEATURE [PartDesign::Pocket] Pocket082
  BaseFeature = -> MultiTransform014
  Direction = (0.5,-0.866025,-1e-16)
  Length = 33
  Length2 = 5
  Midplane = true
  Profile = -> Sketch129
  ReferenceAxis = -> Sketch129 [N_Axis]
  Type = 0
  expr: Length = <<main>>.end_face_width + 1mm
FEATURE [PartDesign::Pocket] Pocket006
  BaseFeature = -> Pocket082
  Direction = (-1,2e-16,-2e-16)
  Length = 33
  Length2 = 160
  Midplane = true
  Profile = -> Sketch009
  ReferenceAxis = -> Sketch009 [N_Axis]
  Type = 0
  expr: Length = <<main>>.end_face_width + 1mm
FEATURE [Sketcher::SketchObject] Sketch137
  AttachmentOffset = pos=(0,18.4752,0) rot=(0.935113,-0.250563,-0.250563;1.63783rad)
  ExternalGeometry = -> [Sketch128]
  FullyConstrained = true
  MapMode = 5
  Placement = pos=(-16,-9.2376,0) rot=(0.57735,0.57735,0.57735;2.0944rad)
  Support = -> [Local_CS042]
  expr: .AttachmentOffset.Base.y = -Sketch009.AttachmentOffset.Base.y
  expr: .AttachmentOffset.Rotation.Angle = Sketch009.AttachmentOffset.Rotation.Angle
  expr: .AttachmentOffset.Rotation.Axis = Sketch009.AttachmentOffset.Rotation.Axis
  expr: Constraints[20] = Sketch009.Constraints[20]
  expr: Constraints[21] = Sketch009.Constraints[21]
  expr: Constraints[34] = Sketch009.Constraints[34]
  expr: Constraints[35] = Sketch009.Constraints[35]
  expr: Constraints[7] = Sketch009.Constraints[7]
  sketch-geometry (18):
    g0: LineSegment StartX=0 StartY=0 StartZ=0 EndX=0 EndY=157 EndZ=0
    g1: LineSegment StartX=190.484 StartY=160.105 StartZ=0 EndX=190.484 EndY=127 EndZ=0
    g2: LineSegment StartX=185.484 StartY=122 StartZ=0 EndX=181.372 EndY=122 EndZ=0
    g3: LineSegment StartX=176.526 StartY=118.232 StartZ=0 EndX=146.477 EndY=0 EndZ=0
    g4: LineSegment StartX=146.477 StartY=0 StartZ=0 EndX=0 EndY=0 EndZ=0
    g5: ArcOfCircle CenterX=185.484 CenterY=160.105 CenterZ=0 NormalX=0 NormalY=0 NormalZ=1 AngleXU=0 Radius=5 StartAngle=1.2868e-12 EndAngle=1.5708
    g6: GeomPoint X=190.484 Y=165.105 Z=0
    g7: ArcOfCircle CenterX=185.484 CenterY=127 CenterZ=0 NormalX=0 NormalY=0 NormalZ=1 AngleXU=0 Radius=5 StartAngle=4.71239 EndAngle=6.28319
    g8: GeomPoint X=190.484 Y=122 Z=0
    g9: ArcOfCircle CenterX=181.372 CenterY=117 CenterZ=0 NormalX=0 NormalY=0 NormalZ=1 AngleXU=0 Radius=5 StartAngle=1.5708 EndAngle=2.89271
    g10: GeomPoint X=177.484 Y=122 Z=0
    g11: LineSegment StartX=82.2376 StartY=116.654 StartZ=0 EndX=174.884 EndY=124.76 EndZ=0
    g12: LineSegment StartX=174.884 StartY=124.76 StartZ=0 EndX=171.354 EndY=165.105 EndZ=0
    g13: LineSegment StartX=171.354 StartY=165.105 StartZ=0 EndX=78.7078 EndY=157 EndZ=0
    g14: LineSegment StartX=78.7078 StartY=157 StartZ=0 EndX=82.2376 EndY=116.654 EndZ=0
    g15: LineSegment StartX=0 StartY=157 StartZ=0 EndX=78.7078 EndY=157 EndZ=0
    g16: LineSegment StartX=171.354 StartY=165.105 StartZ=0 EndX=185.484 EndY=165.105 EndZ=0
    g17: LineSegment StartX=208.395 StartY=149.752 StartZ=0 EndX=190.484 EndY=149.752 EndZ=0
  constraints (44):
    c: Coincident(g-1,g0)
    c: Vertical(g0)
    c: Vertical(g1)
    c: Horizontal(g2)
    c: PointOnObject(g3,g-1)
    c: Coincident(g3,g4)
    c: Coincident(g4,g0)
    c: DistanceY(g0,g0) = 157
    c: PointOnObject(g6,g1)
    c: Tangent(g1,g5) = 1.5708
    c: PointOnObject(g8,g2)
    c: PointOnObject(g8,g1)
    c: Tangent(g2,g7) = 1.5708
    c: Tangent(g1,g7) = 1.5708
    c: PointOnObject(g10,g3)
    c: PointOnObject(g10,g2)
    c: Tangent(g3,g9) = -1.5708
    c: Tangent(g2,g9) = -1.5708
    c: Equal(g9,g7)
    c: Equal(g7,g5)
    c: Diameter(g7) = 10
    c: Distance(g8,g10) = 13
    c: Coincident(g11,g12)
    c: Coincident(g12,g13)
    c: Coincident(g13,g14)
    c: Coincident(g14,g11)
    c: Coincident(g15,g0)
    c: Coincident(g15,g13)
    c: Coincident(g16,g12)
    c: Horizontal(g16)
    c: Tangent(g16,g5) = 1.5708
    c: PointOnObject(g6,g16)
    c: PointOnObject(g17,g1)
    c: Horizontal(g17)
    c: DistanceX(g17) = 208.395
    c: DistanceY(g17) = 149.752
    c: Coincident(g11,g-3)
    c: Angle(g3,g-1) = 1.81968
    c: Distance(g11,g3) = 3.2
    c: DistanceY(g8,g14) = 35
    c: Coincident(g11,g-4)
    c: Perpendicular(g12,g13)
    c: Perpendicular(g14,g11)
    c: Coincident(g12,g-5)
FEATURE [PartDesign::Pocket] Pocket094
  BaseFeature = -> Pocket006
  Direction = (-1,1e-16,-4e-16)
  Length = 5
  Length2 = 5
  Profile = -> Sketch137
  ReferenceAxis = -> Sketch137 [N_Axis]
  Reversed = true
  Type = 0
FEATURE [PartDesign::Mirrored] Mirrored002
  BaseFeature = -> Pocket094
  MirrorPlane = -> DatumPlane014
  Originals = -> [Pocket006,Pocket094]
FEATURE [PartDesign::Body] Body001  label="Body001_material_0.30ansi"
  Group = -> [Local_CS,Local_CS011,Sketch003,BaseBend001,Local_CS012,DatumPlane011,DatumPlane012,Local_CS035,Local_CS036,Local_CS037,Local_CS038,Sketch112,Sketch113,Sketch128,Pocket081,Local_CS039,PolarPattern016,Bend,Pocket007,Pocket091,Sketch129,Local_CS041,Sketch130,Sketch136,Pocket093,Pocket083,MultiTransform014,Mirrored040,PolarPattern017,Local_CS042,Pocket082,Pocket006,Sketch137,Pocket094,Mirrored002,+61 more]
  Origin = -> Origin001
  Tip = -> Pocket094
COMPONENT P2 — geometry summary ("module001"; no construction recipe available for this part):
  bounding box: 170.0 x 148.0 x 41.1 mm
  tessellated surface: 9,330 triangles
  volume: 46706 mm^3 (5% of its bounding box)
  symmetry: mirror-symmetric across its y mid-plane
COMPONENT P3 — recipe-attached ("basin_cover", modeled in this document).
Construction recipe (the document's own serialized feature program — sketch geometry with constraints, then the solid features built on it; lengths are millimeters unless a unit is written):

FEATURE [Sketcher::SketchObject] Sketch047
  FullyConstrained = true
  MapMode = 5
  Support = -> [XY_Plane015]
  expr: Constraints[16] = Sketch003.Constraints.max_r
  expr: Constraints[20] = <<main>>.work_plane_width
  sketch-geometry (8):
    g0: ArcOfCircle CenterX=0 CenterY=18.4752 CenterZ=0 NormalX=0 NormalY=0 NormalZ=1 AngleXU=0 Radius=60 StartAngle=0.539993 EndAngle=1.5708
    g1: ArcOfCircle CenterX=52.3205 CenterY=49.8371 CenterZ=0 NormalX=0 NormalY=0 NormalZ=1 AngleXU=0 Radius=1 StartAngle=3.68159 EndAngle=5.23599
    g2: LineSegment StartX=52.8205 StartY=48.9711 StartZ=0 EndX=172.268 EndY=117.934 EndZ=0
    g3: ArcOfCircle CenterX=171.768 CenterY=118.8 CenterZ=0 NormalX=0 NormalY=0 NormalZ=1 AngleXU=0 Radius=1 StartAngle=5.23599 EndAngle=6.88827
    g4: ArcOfCircle CenterX=0 CenterY=0 CenterZ=0 NormalX=0 NormalY=0 NormalZ=1 AngleXU=0 Radius=209.848 StartAngle=0.605088 EndAngle=1.5708
    g5: LineSegment StartX=3.7e-15 StartY=78.4752 StartZ=0 EndX=1.28e-14 EndY=209.848 EndZ=0
    g6: LineSegment StartX=52.8205 StartY=48.9711 StartZ=0 EndX=0 EndY=18.4752 EndZ=0
    g7: GeomPoint X=173.205 Y=118.475 Z=0
  constraints (22):
    c: PointOnObject(g0,g-2)
    c: PointOnObject(g4,g-2)
    c: Diameter(g1) = 2
    c: Diameter(g3) = 2
    c: Tangent(g1,g0) = 1.5708
    c: Tangent(g3,g2) = -1.5708
    c: Angle(g2,g-1) = 2.61799
    c: Coincident(g5,g0)
    c: Coincident(g5,g4)
    c: Tangent(g1,g2) = -1.5708
    c: Coincident(g6,g1)
    c: Tangent(g6,g2)
    c: Coincident(g6,g0)
    c: Diameter(g0) = 120
    c: PointOnObject(g7,g4)
    c: PointOnObject(g7,g2)
    c: DistanceY(g4) = 209.848
    c: Distance(g4,g0) = 18.4752  'major_r_offset'
    c: Coincident(g4,g-1)
    c: PointOnObject(g0,g-2)
    c: Distance(g0,g7) = 200
    c: Tangent(g3,g4) = -1.5708
FEATURE [PartDesign::Pad] Pad012
  Direction = (0,0,1)
  Length = 3
  Length2 = 10
  Profile = -> Sketch047
  ReferenceAxis = -> Sketch047 [N_Axis]
  Type = 0
FEATURE [PartDesign::CoordinateSystem] Local_CS013
  AttacherType = Attacher::AttachEngine3D
  MapMode = 5
  Support = -> [XY_Plane015]
FEATURE [PartDesign::CoordinateSystem] Local_CS016
  AttacherType = Attacher::AttachEngine3D
  AttachmentOffset = pos=(0,0,0) rot=(0,0,1;0.523599rad)
  MapMode = 5
  Placement = pos=(0,0,0) rot=(0,0,1;0.523599rad)
  Support = -> [XY_Plane015]
FEATURE [PartDesign::Plane] DatumPlane015
  Length = 495.835
  MapMode = 5
  Placement = pos=(0,0,0) rot=(0,0,1;0.523599rad)
  ResizeMode = 0
  Support = -> [Local_CS016]
  Width = 455.324
FEATURE [PartDesign::Plane] DatumPlane016
  Length = 403.575
  MapMode = 4
  Placement = pos=(86.82,84.1932,0) rot=(0.377964,0.654654,0.654654;2.41886rad)
  ResizeMode = 0
  Width = 77.428
FEATURE [PartDesign::CoordinateSystem] Local_CS026
  AttacherType = Attacher::AttachEngine3D
  AttachmentOffset = pos=(0,18.4752,0) rot=(0,0,1;0.523599rad)
  MapMode = 5
  Placement = pos=(0,18.4752,0) rot=(0,0,1;0.523599rad)
  Support = -> [XY_Plane015]
  expr: .AttachmentOffset.Base.y = Sketch047.Constraints.major_r_offset
FEATURE [PartDesign::SubShapeBinder] Binder041
  BindCopyOnChange = 0
  BindMode = 0
  ClaimChildren = false
  Context = -> Model [Body001003005002.Binder041.]
  Fuse = false
  MakeFace = true
  OffsetFill = false
  OffsetIntersection = false
  OffsetJoinType = 0
  OffsetOpenResult = false
  PartialLoad = false
  Relative = false
  Support = -> [Body001003005003013[Pocket041.Sketch083.]]
  _Version = 2
FEATURE [PartDesign::SubShapeBinder] Binder042
  BindCopyOnChange = 0
  BindMode = 0
  ClaimChildren = false
  Context = -> Model [Body001003005002.Binder042.]
  Fuse = false
  MakeFace = true
  OffsetFill = false
  OffsetIntersection = false
  OffsetJoinType = 0
  OffsetOpenResult = false
  PartialLoad = false
  Relative = false
  Support = -> [Body001003005003013[Pocket042.Sketch084.]]
  _Version = 2
FEATURE [PartDesign::SubShapeBinder] Binder043
  BindCopyOnChange = 0
  BindMode = 0
  ClaimChildren = false
  Context = -> Model [Body001003005002.Binder043.]
  Fuse = false
  MakeFace = true
  OffsetFill = false
  OffsetIntersection = false
  OffsetJoinType = 0
  OffsetOpenResult = false
  PartialLoad = false
  Placement = pos=(85.2799,83.8774,0) rot=(0,0,1;0.523599rad)
  Relative = false
  Support = -> [Body001[Sketch043.]]
  _Version = 2
  expr: Placement = Local_CS043.Placement
FEATURE [PartDesign::CoordinateSystem] Local_CS043
  AttacherType = Attacher::AttachEngine3D
  AttachmentOffset = pos=(115.793,30,0) rot=(0,0,1;0rad)
  MapMode = 5
  Placement = pos=(85.2799,83.8774,0) rot=(0,0,1;0.523599rad)
  Support = -> [Local_CS016]
  expr: .AttachmentOffset.Base.x = Local_CS012.AttachmentOffset.Base.y
FEATURE [PartDesign::Pocket] Pocket086
  BaseFeature = -> Pad012
  Direction = (0,0,-1)
  Length = 5
  Length2 = 5
  Midplane = true
  Profile = -> Binder043
  Type = 1
FEATURE [PartDesign::CoordinateSystem] Local_CS044
  AttacherType = Attacher::AttachEngine3D
  AttachmentOffset = pos=(115.793,13,0) rot=(0,0,1;0rad)
  MapMode = 5
  Placement = pos=(93.7799,69.155,0) rot=(0,0,1;0.523599rad)
  Support = -> [Local_CS016]
  expr: .AttachmentOffset.Base.x = Local_CS043.AttachmentOffset.Base.x
  expr: .AttachmentOffset.Base.y = <<main>>.end_face_width / 2 - <<main>>.thickness
FEATURE [PartDesign::SubShapeBinder] Binder046
  BindCopyOnChange = 0
  BindMode = 0
  ClaimChildren = false
  Context = -> Model [Body001003005002.Binder046.]
  Fuse = false
  MakeFace = true
  OffsetFill = false
  OffsetIntersection = false
  OffsetJoinType = 0
  OffsetOpenResult = false
  PartialLoad = false
  Placement = pos=(93.7799,69.155,0) rot=(0,0,1;0.523599rad)
  Relative = false
  Support = -> [Body001[Pocket073.Sketch073.]]
  _Version = 2
  expr: Placement = Local_CS044.Placement
FEATURE [PartDesign::Pocket] Pocket089
  BaseFeature = -> Pocket086
  Direction = (0,0,-1)
  Length = 5
  Length2 = 5
  Midplane = true
  Profile = -> Binder046
  Type = 1
FEATURE [PartDesign::Mirrored] Mirrored014
  BaseFeature = -> Pocket089
  MirrorPlane = -> Sketch047 [V_Axis]
  Originals = -> [Pad012,Pocket086,Pocket089]
  Refine = true
FEATURE [PartDesign::Pocket] Pocket084
  BaseFeature = -> Mirrored014
  Direction = (0,0,-1)
  Length = 5
  Length2 = 5
  Midplane = true
  Profile = -> Binder041
  Type = 1
FEATURE [PartDesign::Pocket] Pocket085
  BaseFeature = -> Pocket084
  Direction = (0,0,-1)
  Length = 5
  Length2 = 5
  Midplane = true
  Profile = -> Binder042
  Type = 1
FEATURE [PartDesign::Body] Body001003005  label="basin_cover"
  Group = -> [Sketch047,Pad012,Pocket086,Pocket089,Mirrored014,Local_CS013,Local_CS016,DatumPlane015,DatumPlane016,Local_CS026,Binder041,Binder042,Pocket084,Pocket085,Binder043,Local_CS043,Local_CS044,Binder046]
  Origin = -> Origin014
  Placement = pos=(0,0,0) rot=(0,0,1;1.0472rad)
  Tip = -> Pocket085
COMPONENT P4 — recipe-attached ("basement", modeled in this document).
Construction recipe (the document's own serialized feature program — sketch geometry with constraints, then the solid features built on it; lengths are millimeters unless a unit is written):

FEATURE [Sketcher::SketchObject] Sketch048
  FullyConstrained = true
  MapMode = 5
  Support = -> [XY_Plane016]
  expr: Constraints[1] = Sketch003.Constraints.max_r + 2.5mm
  sketch-geometry (1):
    g0: Circle CenterX=0 CenterY=0 CenterZ=0 NormalX=0 NormalY=0 NormalZ=1 AngleXU=0 Radius=212.348
  constraints (2):
    c: Coincident(g0,g-1)
    c: Radius(g0) = 212.348
FEATURE [PartDesign::Pad] Pad013
  Direction = (0,0,1)
  Length = 3
  Length2 = 10
  Profile = -> Sketch048
  ReferenceAxis = -> Sketch048 [N_Axis]
  Type = 0
  expr: Length = <<main>>.thickness
FEATURE [Sketcher::SketchObject] Sketch049
  AttachmentOffset = pos=(0,196.563,0) rot=(0,0,1;0rad)
  FullyConstrained = true
  MapMode = 5
  Placement = pos=(0,196.563,0) rot=(0,0,1;0rad)
  Support = -> [XY_Plane016]
  expr: .AttachmentOffset.Base.y = Sketch003.Constraints.total_petal_length - .Constraints.cut_width / 2 - 3.175mm - <<main>>.thickness
  expr: Constraints[10] = <<main>>.inner_width / 2
  expr: Constraints[14] = -<<main>>.inner_width / 2
  sketch-geometry (9):
    g0: ArcOfCircle CenterX=-13 CenterY=8.0875 CenterZ=0 NormalX=0 NormalY=0 NormalZ=1 AngleXU=0 Radius=1.5875 StartAngle=1.5708 EndAngle=4.71239
    g1: LineSegment StartX=-13 StartY=6.5 StartZ=0 EndX=9.825 EndY=6.5 EndZ=0
    g2: LineSegment StartX=9.825 StartY=6.5 StartZ=0 EndX=9.825 EndY=0 EndZ=0
    g3: LineSegment StartX=9.825 StartY=0 StartZ=0 EndX=13 EndY=0 EndZ=0
    g4: LineSegment StartX=13 StartY=0 StartZ=0 EndX=13 EndY=6.5 EndZ=0
    g5: LineSegment StartX=-13 StartY=9.675 StartZ=0 EndX=9.825 EndY=9.675 EndZ=0
    g6: ArcOfCircle CenterX=9.825 CenterY=6.5 CenterZ=0 NormalX=0 NormalY=0 NormalZ=1 AngleXU=0 Radius=3.175 StartAngle=1.117e-13 EndAngle=1.5708
    g7: GeomPoint X=9.825 Y=-6.5 Z=0
    g8: GeomPoint X=9.825 Y=-9.675 Z=0
  constraints (21):
    c: Horizontal(g1)
    c: PointOnObject(g2,g-1)
    c: Vertical(g2)
    c: Coincident(g3,g2)
    c: PointOnObject(g3,g-1)
    c: Coincident(g4,g3)
    c: Vertical(g4)
    c: Horizontal(g5)
    c: Tangent(g6,g4) = -1.5708
    c: Tangent(g6,g5) = 1.5708
    c: DistanceX(g3) = 13
    c: Tangent(g1,g0) = -1.5708
    c: Tangent(g5,g0) = 1.5708
    c: Diameter(g0) = 3.175
    c: DistanceX(g0) = -13
    c: Coincident(g6,g2)
    c: Coincident(g2,g1)
    c: Symmetric(g7,g1,g2)
    c: DistanceY(g7,g1) = 13  'cut_width'
    c: Symmetric(g8,g5,g2)
    c: DistanceY(g8,g5) = 19.35  'total_width'
FEATURE [Sketcher::SketchObject] Sketch050
  AttachmentOffset = pos=(0,196.563,0) rot=(0,0,1;0rad)
  FullyConstrained = true
  MapMode = 5
  Placement = pos=(0,196.563,0) rot=(0,0,1;0rad)
  Support = -> [XY_Plane016]
  expr: .AttachmentOffset.Base.y = Sketch049.AttachmentOffset.Base.y
  expr: .Constraints.cut_width = Sketch049.Constraints[18]
  expr: Constraints[10] = Sketch049.Constraints[10]
  expr: Constraints[13] = Sketch049.Constraints[13]
  expr: Constraints[14] = Sketch049.Constraints[14]
  expr: Constraints[29] = Sketch049.Constraints[10]
  expr: Constraints[32] = Sketch049.Constraints[13]
  expr: Constraints[33] = Sketch049.Constraints[14]
  sketch-geometry (17):
    g0: LineSegment StartX=-13 StartY=-8.0875 StartZ=0 EndX=-13 EndY=8.0875 EndZ=0
    g1: ArcOfCircle CenterX=-13 CenterY=8.0875 CenterZ=0 NormalX=0 NormalY=0 NormalZ=1 AngleXU=0 Radius=1.5875 StartAngle=1.5708 EndAngle=4.71239
    g2: LineSegment StartX=-13 StartY=6.5 StartZ=0 EndX=9.825 EndY=6.5 EndZ=0
    g3: LineSegment StartX=9.825 StartY=6.5 StartZ=0 EndX=9.825 EndY=0 EndZ=0
    g4: LineSegment StartX=9.825 StartY=0 StartZ=0 EndX=13 EndY=0 EndZ=0
    g5: LineSegment StartX=13 StartY=0 StartZ=0 EndX=13 EndY=6.5 EndZ=0
    g6: LineSegment StartX=-13 StartY=9.675 StartZ=0 EndX=9.825 EndY=9.675 EndZ=0
    g7: ArcOfCircle CenterX=9.825 CenterY=6.5 CenterZ=0 NormalX=0 NormalY=0 NormalZ=1 AngleXU=0 Radius=3.175 StartAngle=1.742e-13 EndAngle=1.5708
    g8: GeomPoint X=9.825 Y=-6.5 Z=0
    g9: ArcOfCircle CenterX=-11.5 CenterY=11.5875 CenterZ=0 NormalX=0 NormalY=0 NormalZ=1 AngleXU=0 Radius=1.5875 StartAngle=1.5708 EndAngle=4.71239
    g10: LineSegment StartX=-11.5 StartY=10 StartZ=0 EndX=9.825 EndY=10 EndZ=0
    g11: LineSegment StartX=9.825 StartY=10 StartZ=0 EndX=9.825 EndY=0 EndZ=0
    g12: LineSegment StartX=9.825 StartY=0 StartZ=0 EndX=13 EndY=0 EndZ=0
    g13: LineSegment StartX=13 StartY=0 StartZ=0 EndX=13 EndY=10 EndZ=0
    g14: LineSegment StartX=-11.5 StartY=13.175 StartZ=0 EndX=9.825 EndY=13.175 EndZ=0
    g15: ArcOfCircle CenterX=9.825 CenterY=10 CenterZ=0 NormalX=0 NormalY=0 NormalZ=1 AngleXU=0 Radius=3.175 StartAngle=1e-16 EndAngle=1.5708
    g16: GeomPoint X=9.825 Y=-10 Z=0
  constraints (40):
    c: Horizontal(g2)
    c: PointOnObject(g3,g-1)
    c: Vertical(g3)
    c: Coincident(g4,g3)
    c: PointOnObject(g4,g-1)
    c: Coincident(g5,g4)
    c: Vertical(g5)
    c: Horizontal(g6)
    c: Tangent(g7,g5) = -1.5708
    c: Tangent(g7,g6) = 1.5708
    c: DistanceX(g4) = 13
    c: Tangent(g2,g1) = -1.5708
    c: Tangent(g6,g1) = 1.5708
    c: Diameter(g1) = 3.175
    c: DistanceX(g1) = -13
    c: Coincident(g7,g3)
    c: Coincident(g3,g2)
    c: Symmetric(g8,g2,g3)
    c: DistanceY(g8,g2) = 13  'cut_width'
    c: Horizontal(g10)
    c: PointOnObject(g11,g-1)
    c: Vertical(g11)
    c: Coincident(g12,g11)
    c: PointOnObject(g12,g-1)
    c: Coincident(g13,g12)
    c: Vertical(g13)
    c: Horizontal(g14)
    c: Tangent(g15,g13) = -1.5708
    c: Tangent(g15,g14) = 1.5708
    c: DistanceX(g12) = 13
    c: Tangent(g10,g9) = -1.5708
    c: Tangent(g14,g9) = 1.5708
    c: Diameter(g9) = 3.175
    c: DistanceX(g9) = -11.5
    c: Coincident(g15,g11)
    c: Coincident(g11,g10)
    c: Symmetric(g16,g10,g11)
    c: DistanceY(g16,g10) = 20  'cut_width'
    c: Coincident(g0,g1)
    c: Symmetric(g0,g0,g-1)
FEATURE [PartDesign::CoordinateSystem] Local_CS017
  AttacherType = Attacher::AttachEngine3D
  AttachmentOffset = pos=(0,0,3) rot=(0,0,1;0rad)
  MapMode = 5
  Placement = pos=(0,0,3) rot=(0,0,1;0rad)
  Support = -> [XY_Plane016]
  expr: .AttachmentOffset.Base.z = <<main>>.thickness
FEATURE [PartDesign::SubShapeBinder] Binder004
  AttacherType = Attacher::AttachEngine3D
  AttachmentOffset = pos=(0,196.563,0) rot=(0,0,1;3.14159rad)
  BindCopyOnChange = 0
  BindMode = 0
  ClaimChildren = false
  Context = -> Model [Body001003005003002.Binder004.]
  Fuse = false
  MakeFace = true
  MapMode = 5
  OffsetFill = false
  OffsetIntersection = false
  OffsetJoinType = 0
  OffsetOpenResult = false
  PartialLoad = false
  Placement = pos=(0,180.388,0) rot=(0,0,1;3.14159rad)
  Relative = false
  _Version = 2
  expr: .AttachmentOffset.Base.y = <<main>>.work_plane_width + Sketch003.Constraints.petal_offset - <<main>>.thickness - 3.175mm - Sketch049.Constraints.cut_width / 2
  expr: .Placement.Base.y = Sketch049.AttachmentOffset.Base.y - Sketch049.Constraints.cut_width - 3.175mm
FEATURE [PartDesign::Plane] DatumPlane017
  Length = 453.129
  MapMode = 3
  Placement = pos=(0,180.388,0) rot=(0,0.707107,0.707107;3.14159rad)
  ResizeMode = 0
  Support = -> [Binder004]
  Width = 79.1207
FEATURE [Sketcher::SketchObject] Sketch051
  AttachmentOffset = pos=(0,180.388,0) rot=(0,0,1;0rad)
  FullyConstrained = true
  MapMode = 5
  Placement = pos=(0,180.388,0) rot=(0,0,1;0rad)
  Support = -> [XY_Plane016]
  expr: .AttachmentOffset.Base.y = Binder004.Placement.Base.y
  expr: .Constraints.cut_width = Sketch049.Constraints[18]
  expr: Constraints[10] = Sketch049.Constraints[10]
  expr: Constraints[13] = Sketch049.Constraints[13]
  expr: Constraints[14] = Sketch049.Constraints[14]
  sketch-geometry (9):
    g0: ArcOfCircle CenterX=-11.5 CenterY=8.0875 CenterZ=0 NormalX=0 NormalY=0 NormalZ=1 AngleXU=0 Radius=1.5875 StartAngle=1.5708 EndAngle=4.71239
    g1: LineSegment StartX=-11.5 StartY=6.5 StartZ=0 EndX=9.825 EndY=6.5 EndZ=0
    g2: LineSegment StartX=9.825 StartY=6.5 StartZ=0 EndX=9.825 EndY=0 EndZ=0
    g3: LineSegment StartX=9.825 StartY=0 StartZ=0 EndX=13 EndY=0 EndZ=0
    g4: LineSegment StartX=13 StartY=0 StartZ=0 EndX=13 EndY=6.5 EndZ=0
    g5: LineSegment StartX=-11.5 StartY=9.675 StartZ=0 EndX=9.825 EndY=9.675 EndZ=0
    g6: ArcOfCircle CenterX=9.825 CenterY=6.5 CenterZ=0 NormalX=0 NormalY=0 NormalZ=1 AngleXU=0 Radius=3.175 StartAngle=0 EndAngle=1.5708
    g7: GeomPoint X=9.825 Y=-6.5 Z=0
    g8: LineSegment StartX=11.5 StartY=8.0875 StartZ=0 EndX=11.5 EndY=-8.0875 EndZ=0
  constraints (22):
    c: Horizontal(g1)
    c: PointOnObject(g2,g-1)
    c: Vertical(g2)
    c: Coincident(g3,g2)
    c: PointOnObject(g3,g-1)
    c: Coincident(g4,g3)
    c: Vertical(g4)
    c: Horizontal(g5)
    c: Tangent(g6,g4) = -1.5708
    c: Tangent(g6,g5) = 1.5708
    c: DistanceX(g3) = 13
    c: Tangent(g1,g0) = -1.5708
    c: Tangent(g5,g0) = 1.5708
    c: Diameter(g0) = 3.175
    c: DistanceX(g0) = -11.5
    c: Coincident(g6,g2)
    c: Coincident(g2,g1)
    c: Symmetric(g7,g1,g2)
    c: DistanceY(g7,g1) = 13  'cut_width'
    c: Vertical(g8)
    c: Symmetric(g0,g8,g-1)
    c: Horizontal(g8,g0)
FEATURE [PartDesign::SubShapeBinder] Binder005
  AttacherType = Attacher::AttachEngine3D
  AttachmentOffset = pos=(0,0,0) rot=(0,0,1;1.0472rad)
  BindCopyOnChange = 0
  BindMode = 0
  ClaimChildren = false
  Context = -> Body001003005003 [Binder005.]
  Fuse = false
  MakeFace = true
  MapMode = 5
  OffsetFill = false
  OffsetIntersection = false
  OffsetJoinType = 0
  OffsetOpenResult = false
  PartialLoad = false
  Placement = pos=(0,0,0) rot=(0,0,1;1.0472rad)
  Relative = false
  _Version = 2
FEATURE [PartDesign::Plane] DatumPlane018
  Length = 613.419
  MapMode = 4
  Placement = pos=(0,0,0) rot=(0.186157,0.694747,0.694747;2.77349rad)
  ResizeMode = 0
  Support = -> [Binder005]
  Width = 84.0405
FEATURE [Sketcher::SketchObject] Sketch057
  AttachmentOffset = pos=(196.563,-11.5,0) rot=(0,0,1;0rad)
  FullyConstrained = true
  MapMode = 5
  Placement = pos=(4.62e-14,196.563,-11.5) rot=(0.57735,0.57735,0.57735;2.0944rad)
  Support = -> [YZ_Plane015]
  expr: .AttachmentOffset.Base.x = Sketch049.AttachmentOffset.Base.y
  expr: .AttachmentOffset.Base.y = -23mm / 2
  expr: Constraints[1] = <<main>>.rivet_d
  sketch-geometry (1):
    g0: Circle CenterX=0 CenterY=0 CenterZ=0 NormalX=0 NormalY=0 NormalZ=1 AngleXU=0 Radius=1.7
  constraints (2):
    c: Coincident(g0,g-1)
    c: Diameter(g0) = 3.4
FEATURE [Sketcher::SketchObject] Sketch058
  AttachmentOffset = pos=(180.388,-11.5,0) rot=(0,0,1;0rad)
  FullyConstrained = true
  MapMode = 5
  Placement = pos=(4.26e-14,180.388,-11.5) rot=(0.57735,0.57735,0.57735;2.0944rad)
  Support = -> [YZ_Plane015]
  expr: .AttachmentOffset.Base.x = Binder004.Placement.Base.y
  expr: .AttachmentOffset.Base.y = Sketch057.AttachmentOffset.Base.y
  expr: Constraints[1] = <<main>>.rivet_d
  sketch-geometry (1):
    g0: Circle CenterX=0 CenterY=0 CenterZ=0 NormalX=0 NormalY=0 NormalZ=1 AngleXU=0 Radius=1.7
  constraints (2):
    c: Coincident(g0,g-1)
    c: Diameter(g0) = 3.4
FEATURE [PartDesign::Pocket] Pocket027
  BaseFeature = -> Pad013
  Direction = (-1,2e-16,-3e-16)
  Length = 5
  Length2 = 5
  Midplane = true
  Profile = -> Sketch058
  ReferenceAxis = -> Sketch058 [N_Axis]
  Type = 1
FEATURE [PartDesign::CoordinateSystem] Local_CS021
  AttacherType = Attacher::AttachEngine3D
  AttachmentOffset = pos=(0,0,0) rot=(0,0,1;2.0944rad)
  MapMode = 5
  Placement = pos=(0,0,0) rot=(0,0,1;2.0944rad)
  Support = -> [XY_Plane016]
FEATURE [PartDesign::CoordinateSystem] Local_CS022
  AttacherType = Attacher::AttachEngine3D
  AttachmentOffset = pos=(0,0,0) rot=(0,0,-1;2.0944rad)
  MapMode = 5
  Placement = pos=(0,0,0) rot=(0,0,-1;2.0944rad)
  Support = -> [XY_Plane016]
FEATURE [PartDesign::Plane] DatumPlane019
  Length = 695.392
  MapMode = 5
  Placement = pos=(0,0,0) rot=(0,0,1;2.0944rad)
  ResizeMode = 0
  Support = -> [Local_CS021]
  Width = 695.266
FEATURE [PartDesign::Plane] DatumPlane020
  Length = 695.392
  MapMode = 5
  Placement = pos=(0,0,0) rot=(0,0,-1;2.0944rad)
  ResizeMode = 0
  Support = -> [Local_CS022]
  Width = 695.266
FEATURE [Sketcher::SketchObject] Sketch061
  AttachmentOffset = pos=(0,196.563,0) rot=(0,0,1;0rad)
  FullyConstrained = true
  MapMode = 5
  Placement = pos=(-170.228,-98.2813,0) rot=(0,0,1;2.0944rad)
  Support = -> [DatumPlane019]
  expr: .AttachmentOffset.Base.y = Sketch050.Placement.Base.y
  expr: .Constraints.cut_width = 13
  expr: Constraints[10] = Sketch050.Constraints[10]
  expr: Constraints[13] = Sketch050.Constraints[13]
  expr: Constraints[14] = Sketch050.Constraints[14]
  expr: Constraints[29] = Sketch050.Constraints[29]
  expr: Constraints[32] = Sketch050.Constraints[32]
  expr: Constraints[33] = Sketch050.Constraints[33]
  sketch-geometry (17):
    g0: LineSegment StartX=-13 StartY=-8.0875 StartZ=0 EndX=-13 EndY=8.0875 EndZ=0
    g1: ArcOfCircle CenterX=-13 CenterY=8.0875 CenterZ=0 NormalX=0 NormalY=0 NormalZ=1 AngleXU=0 Radius=1.5875 StartAngle=1.5708 EndAngle=4.71239
    g2: LineSegment StartX=-13 StartY=6.5 StartZ=0 EndX=9.825 EndY=6.5 EndZ=0
    g3: LineSegment StartX=9.825 StartY=6.5 StartZ=0 EndX=9.825 EndY=0 EndZ=0
    g4: LineSegment StartX=9.825 StartY=0 StartZ=0 EndX=13 EndY=0 EndZ=0
    g5: LineSegment StartX=13 StartY=0 StartZ=0 EndX=13 EndY=6.5 EndZ=0
    g6: LineSegment StartX=-13 StartY=9.675 StartZ=0 EndX=9.825 EndY=9.675 EndZ=0
    g7: ArcOfCircle CenterX=9.825 CenterY=6.5 CenterZ=0 NormalX=0 NormalY=0 NormalZ=1 AngleXU=0 Radius=3.175 StartAngle=1.743e-13 EndAngle=1.5708
    g8: GeomPoint X=9.825 Y=-6.5 Z=0
    g9: ArcOfCircle CenterX=-11.5 CenterY=11.5875 CenterZ=0 NormalX=0 NormalY=0 NormalZ=1 AngleXU=0 Radius=1.5875 StartAngle=1.5708 EndAngle=4.71239
    g10: LineSegment StartX=-11.5 StartY=10 StartZ=0 EndX=9.825 EndY=10 EndZ=0
    g11: LineSegment StartX=9.825 StartY=10 StartZ=0 EndX=9.825 EndY=0 EndZ=0
    g12: LineSegment StartX=9.825 StartY=0 StartZ=0 EndX=13 EndY=0 EndZ=0
    g13: LineSegment StartX=13 StartY=0 StartZ=0 EndX=13 EndY=10 EndZ=0
    g14: LineSegment StartX=-11.5 StartY=13.175 StartZ=0 EndX=9.825 EndY=13.175 EndZ=0
    g15: ArcOfCircle CenterX=9.825 CenterY=10 CenterZ=0 NormalX=0 NormalY=0 NormalZ=1 AngleXU=0 Radius=3.175 StartAngle=1e-16 EndAngle=1.5708
    g16: GeomPoint X=9.825 Y=-10 Z=0
  constraints (40):
    c: Horizontal(g2)
    c: PointOnObject(g3,g-1)
    c: Vertical(g3)
    c: Coincident(g4,g3)
    c: PointOnObject(g4,g-1)
    c: Coincident(g5,g4)
    c: Vertical(g5)
    c: Horizontal(g6)
    c: Tangent(g7,g5) = -1.5708
    c: Tangent(g7,g6) = 1.5708
    c: DistanceX(g4) = 13
    c: Tangent(g2,g1) = -1.5708
    c: Tangent(g6,g1) = 1.5708
    c: Diameter(g1) = 3.175
    c: DistanceX(g1) = -13
    c: Coincident(g7,g3)
    c: Coincident(g3,g2)
    c: Symmetric(g8,g2,g3)
    c: DistanceY(g8,g2) = 13  'cut_width'
    c: Horizontal(g10)
    c: PointOnObject(g11,g-1)
    c: Vertical(g11)
    c: Coincident(g12,g11)
    c: PointOnObject(g12,g-1)
    c: Coincident(g13,g12)
    c: Vertical(g13)
    c: Horizontal(g14)
    c: Tangent(g15,g13) = -1.5708
    c: Tangent(g15,g14) = 1.5708
    c: DistanceX(g12) = 13
    c: Tangent(g10,g9) = -1.5708
    c: Tangent(g14,g9) = 1.5708
    c: Diameter(g9) = 3.175
    c: DistanceX(g9) = -11.5
    c: Coincident(g15,g11)
    c: Coincident(g11,g10)
    c: Symmetric(g16,g10,g11)
    c: DistanceY(g16,g10) = 20  'cut_width'
    c: Coincident(g0,g1)
    c: Symmetric(g0,g0,g-1)
FEATURE [Sketcher::SketchObject] Sketch062
  AttachmentOffset = pos=(0,196.563,0) rot=(0,0,1;0rad)
  FullyConstrained = true
  MapMode = 5
  Placement = pos=(170.228,-98.2813,0) rot=(0,0,-1;2.0944rad)
  Support = -> [DatumPlane020]
  expr: .Constraints.cut_width = 13
  expr: AttachmentOffset = Sketch050.AttachmentOffset
  expr: Constraints[10] = Sketch050.Constraints[10]
  expr: Constraints[13] = Sketch050.Constraints[13]
  expr: Constraints[14] = Sketch050.Constraints[14]
  expr: Constraints[29] = Sketch050.Constraints[29]
  expr: Constraints[32] = Sketch050.Constraints[32]
  expr: Constraints[33] = Sketch050.Constraints[33]
  sketch-geometry (17):
    g0: LineSegment StartX=-13 StartY=-8.0875 StartZ=0 EndX=-13 EndY=8.0875 EndZ=0
    g1: ArcOfCircle CenterX=-13 CenterY=8.0875 CenterZ=0 NormalX=0 NormalY=0 NormalZ=1 AngleXU=0 Radius=1.5875 StartAngle=1.5708 EndAngle=4.71239
    g2: LineSegment StartX=-13 StartY=6.5 StartZ=0 EndX=9.825 EndY=6.5 EndZ=0
    g3: LineSegment StartX=9.825 StartY=6.5 StartZ=0 EndX=9.825 EndY=0 EndZ=0
    g4: LineSegment StartX=9.825 StartY=0 StartZ=0 EndX=13 EndY=0 EndZ=0
    g5: LineSegment StartX=13 StartY=0 StartZ=0 EndX=13 EndY=6.5 EndZ=0
    g6: LineSegment StartX=-13 StartY=9.675 StartZ=0 EndX=9.825 EndY=9.675 EndZ=0
    g7: ArcOfCircle CenterX=9.825 CenterY=6.5 CenterZ=0 NormalX=0 NormalY=0 NormalZ=1 AngleXU=0 Radius=3.175 StartAngle=1.743e-13 EndAngle=1.5708
    g8: GeomPoint X=9.825 Y=-6.5 Z=0
    g9: ArcOfCircle CenterX=-11.5 CenterY=11.5875 CenterZ=0 NormalX=0 NormalY=0 NormalZ=1 AngleXU=0 Radius=1.5875 StartAngle=1.5708 EndAngle=4.71239
    g10: LineSegment StartX=-11.5 StartY=10 StartZ=0 EndX=9.825 EndY=10 EndZ=0
    g11: LineSegment StartX=9.825 StartY=10 StartZ=0 EndX=9.825 EndY=0 EndZ=0
    g12: LineSegment StartX=9.825 StartY=0 StartZ=0 EndX=13 EndY=0 EndZ=0
    g13: LineSegment StartX=13 StartY=0 StartZ=0 EndX=13 EndY=10 EndZ=0
    g14: LineSegment StartX=-11.5 StartY=13.175 StartZ=0 EndX=9.825 EndY=13.175 EndZ=0
    g15: ArcOfCircle CenterX=9.825 CenterY=10 CenterZ=0 NormalX=0 NormalY=0 NormalZ=1 AngleXU=0 Radius=3.175 StartAngle=1e-16 EndAngle=1.5708
    g16: GeomPoint X=9.825 Y=-10 Z=0
  constraints (40):
    c: Horizontal(g2)
    c: PointOnObject(g3,g-1)
    c: Vertical(g3)
    c: Coincident(g4,g3)
    c: PointOnObject(g4,g-1)
    c: Coincident(g5,g4)
    c: Vertical(g5)
    c: Horizontal(g6)
    c: Tangent(g7,g5) = -1.5708
    c: Tangent(g7,g6) = 1.5708
    c: DistanceX(g4) = 13
    c: Tangent(g2,g1) = -1.5708
    c: Tangent(g6,g1) = 1.5708
    c: Diameter(g1) = 3.175
    c: DistanceX(g1) = -13
    c: Coincident(g7,g3)
    c: Coincident(g3,g2)
    c: Symmetric(g8,g2,g3)
    c: DistanceY(g8,g2) = 13  'cut_width'
    c: Horizontal(g10)
    c: PointOnObject(g11,g-1)
    c: Vertical(g11)
    c: Coincident(g12,g11)
    c: PointOnObject(g12,g-1)
    c: Coincident(g13,g12)
    c: Vertical(g13)
    c: Horizontal(g14)
    c: Tangent(g15,g13) = -1.5708
    c: Tangent(g15,g14) = 1.5708
    c: DistanceX(g12) = 13
    c: Tangent(g10,g9) = -1.5708
    c: Tangent(g14,g9) = 1.5708
    c: Diameter(g9) = 3.175
    c: DistanceX(g9) = -11.5
    c: Coincident(g15,g11)
    c: Coincident(g11,g10)
    c: Symmetric(g16,g10,g11)
    c: DistanceY(g16,g10) = 20  'cut_width'
    c: Coincident(g0,g1)
    c: Symmetric(g0,g0,g-1)
FEATURE [Sketcher::SketchObject] Sketch063
  AttachmentOffset = pos=(0,180.388,0) rot=(0,0,1;0rad)
  FullyConstrained = true
  MapMode = 5
  Placement = pos=(-156.22,-90.1938,0) rot=(0,0,1;2.0944rad)
  Support = -> [DatumPlane019]
  expr: .Constraints.cut_width = Sketch051.Constraints[18]
  expr: AttachmentOffset = Sketch051.AttachmentOffset
  expr: Constraints[10] = Sketch051.Constraints[10]
  expr: Constraints[13] = Sketch051.Constraints[13]
  expr: Constraints[14] = Sketch051.Constraints[14]
  sketch-geometry (9):
    g0: ArcOfCircle CenterX=-11.5 CenterY=8.0875 CenterZ=0 NormalX=0 NormalY=0 NormalZ=1 AngleXU=0 Radius=1.5875 StartAngle=1.5708 EndAngle=4.71239
    g1: LineSegment StartX=-11.5 StartY=6.5 StartZ=0 EndX=9.825 EndY=6.5 EndZ=0
    g2: LineSegment StartX=9.825 StartY=6.5 StartZ=0 EndX=9.825 EndY=0 EndZ=0
    g3: LineSegment StartX=9.825 StartY=0 StartZ=0 EndX=13 EndY=0 EndZ=0
    g4: LineSegment StartX=13 StartY=0 StartZ=0 EndX=13 EndY=6.5 EndZ=0
    g5: LineSegment StartX=-11.5 StartY=9.675 StartZ=0 EndX=9.825 EndY=9.675 EndZ=0
    g6: ArcOfCircle CenterX=9.825 CenterY=6.5 CenterZ=0 NormalX=0 NormalY=0 NormalZ=1 AngleXU=0 Radius=3.175 StartAngle=0 EndAngle=1.5708
    g7: GeomPoint X=9.825 Y=-6.5 Z=0
    g8: LineSegment StartX=11.5 StartY=8.0875 StartZ=0 EndX=11.5 EndY=-8.0875 EndZ=0
  constraints (22):
    c: Horizontal(g1)
    c: PointOnObject(g2,g-1)
    c: Vertical(g2)
    c: Coincident(g3,g2)
    c: PointOnObject(g3,g-1)
    c: Coincident(g4,g3)
    c: Vertical(g4)
    c: Horizontal(g5)
    c: Tangent(g6,g4) = -1.5708
    c: Tangent(g6,g5) = 1.5708
    c: DistanceX(g3) = 13
    c: Tangent(g1,g0) = -1.5708
    c: Tangent(g5,g0) = 1.5708
    c: Diameter(g0) = 3.175
    c: DistanceX(g0) = -11.5
    c: Coincident(g6,g2)
    c: Coincident(g2,g1)
    c: Symmetric(g7,g1,g2)
    c: DistanceY(g7,g1) = 13  'cut_width'
    c: Vertical(g8)
    c: Symmetric(g0,g8,g-1)
    c: Horizontal(g8,g0)
FEATURE [Sketcher::SketchObject] Sketch064
  AttachmentOffset = pos=(0,180.388,0) rot=(0,0,1;0rad)
  FullyConstrained = true
  MapMode = 5
  Placement = pos=(156.22,-90.1938,0) rot=(0,0,-1;2.0944rad)
  Support = -> [DatumPlane020]
  expr: .Constraints.cut_width = Sketch051.Constraints[18]
  expr: AttachmentOffset = Sketch051.AttachmentOffset
  expr: Constraints[10] = Sketch051.Constraints[10]
  expr: Constraints[13] = Sketch051.Constraints[13]
  expr: Constraints[14] = Sketch051.Constraints[14]
  sketch-geometry (9):
    g0: ArcOfCircle CenterX=-11.5 CenterY=8.0875 CenterZ=0 NormalX=0 NormalY=0 NormalZ=1 AngleXU=0 Radius=1.5875 StartAngle=1.5708 EndAngle=4.71239
    g1: LineSegment StartX=-11.5 StartY=6.5 StartZ=0 EndX=9.825 EndY=6.5 EndZ=0
    g2: LineSegment StartX=9.825 StartY=6.5 StartZ=0 EndX=9.825 EndY=0 EndZ=0
    g3: LineSegment StartX=9.825 StartY=0 StartZ=0 EndX=13 EndY=0 EndZ=0
    g4: LineSegment StartX=13 StartY=0 StartZ=0 EndX=13 EndY=6.5 EndZ=0
    g5: LineSegment StartX=-11.5 StartY=9.675 StartZ=0 EndX=9.825 EndY=9.675 EndZ=0
    g6: ArcOfCircle CenterX=9.825 CenterY=6.5 CenterZ=0 NormalX=0 NormalY=0 NormalZ=1 AngleXU=0 Radius=3.175 StartAngle=0 EndAngle=1.5708
    g7: GeomPoint X=9.825 Y=-6.5 Z=0
    g8: LineSegment StartX=11.5 StartY=8.0875 StartZ=0 EndX=11.5 EndY=-8.0875 EndZ=0
  constraints (22):
    c: Horizontal(g1)
    c: PointOnObject(g2,g-1)
    c: Vertical(g2)
    c: Coincident(g3,g2)
    c: PointOnObject(g3,g-1)
    c: Coincident(g4,g3)
    c: Vertical(g4)
    c: Horizontal(g5)
    c: Tangent(g6,g4) = -1.5708
    c: Tangent(g6,g5) = 1.5708
    c: DistanceX(g3) = 13
    c: Tangent(g1,g0) = -1.5708
    c: Tangent(g5,g0) = 1.5708
    c: Diameter(g0) = 3.175
    c: DistanceX(g0) = -11.5
    c: Coincident(g6,g2)
    c: Coincident(g2,g1)
    c: Symmetric(g7,g1,g2)
    c: DistanceY(g7,g1) = 13  'cut_width'
    c: Vertical(g8)
    c: Symmetric(g0,g8,g-1)
    c: Horizontal(g8,g0)
FEATURE [Sketcher::SketchObject] Sketch075
  AttachmentOffset = pos=(0,0,0) rot=(0,0,1;3.14159rad)
  FullyConstrained = true
  MapMode = 5
  Placement = pos=(0,0,0) rot=(0,0,1;3.14159rad)
  Support = -> [XY_Plane016]
  expr: Constraints[12] = 186.5mm - 3.175mm
  expr: Constraints[6] = <<main>>.rivet_d
  sketch-geometry (6):
    g0: Circle CenterX=64.8152 CenterY=64.8152 CenterZ=0 NormalX=0 NormalY=0 NormalZ=1 AngleXU=0 Radius=1.7
    g1: Circle CenterX=64.8152 CenterY=-64.8152 CenterZ=0 NormalX=0 NormalY=0 NormalZ=1 AngleXU=0 Radius=1.7
    g2: Circle CenterX=-64.8152 CenterY=-64.8152 CenterZ=0 NormalX=0 NormalY=0 NormalZ=1 AngleXU=0 Radius=1.7
    g3: Circle CenterX=-64.8152 CenterY=64.8152 CenterZ=0 NormalX=0 NormalY=0 NormalZ=1 AngleXU=0 Radius=1.7
    g4: LineSegment StartX=-64.8152 StartY=64.8152 StartZ=0 EndX=64.8152 EndY=64.8152 EndZ=0
    g5: LineSegment StartX=64.8152 StartY=64.8152 StartZ=0 EndX=64.8152 EndY=-64.8152 EndZ=0
  constraints (13):
    c: Symmetric(g3,g0,g-2)
    c: Symmetric(g0,g1,g-1)
    c: Symmetric(g0,g2,g-1)
    c: Equal(g0,g3)
    c: Equal(g0,g2)
    c: Equal(g0,g1)
    c: Diameter(g0) = 3.4
    c: Coincident(g4,g3)
    c: Coincident(g4,g0)
    c: Coincident(g5,g0)
    c: Coincident(g5,g1)
    c: Equal(g5,g4)
    c: Distance(g2,g0) = 183.325
FEATURE [PartDesign::Pocket] Pocket036
  BaseFeature = -> Pocket027
  Direction = (0,0,-1)
  Length = 5
  Length2 = 5
  Midplane = true
  Profile = -> Sketch075
  ReferenceAxis = -> Sketch075 [N_Axis]
  Type = 1
FEATURE [PartDesign::SubShapeBinder] Binder018
  BindCopyOnChange = 0
  BindMode = 0
  ClaimChildren = true
  Context = -> Body001003005003 [Binder018.]
  Fuse = false
  MakeFace = true
  OffsetFill = false
  OffsetIntersection = false
  OffsetJoinType = 0
  OffsetOpenResult = false
  PartialLoad = false
  Relative = false
  Support = -> [Body001003005003012[Pocket039.Sketch080.]]
  _Version = 2
FEATURE [PartDesign::SubShapeBinder] Binder023
  BindCopyOnChange = 0
  BindMode = 0
  ClaimChildren = false
  Context = -> Body001003005003 [Binder023.]
  Fuse = false
  MakeFace = true
  OffsetFill = false
  OffsetIntersection = false
  OffsetJoinType = 0
  OffsetOpenResult = false
  PartialLoad = false
  Relative = true
  Support = -> [Body001003005003013[Pocket042.Sketch084.,Pocket041.Sketch083.]]
  _Version = 2
FEATURE [PartDesign::SubShapeBinder] Binder036
  BindCopyOnChange = 0
  BindMode = 0
  ClaimChildren = false
  Context = -> Body001003005003 [Binder036.]
  Fuse = false
  MakeFace = true
  OffsetFill = false
  OffsetIntersection = false
  OffsetJoinType = 0
  OffsetOpenResult = false
  PartialLoad = false
  Placement = pos=(13,180,0) rot=(0,0,1;1.5708rad)
  Relative = true
  Support = -> [Body_7[Pocket061.Sketch105.]]
  _Version = 2
  expr: .Placement.Base.x = <<main>>.end_face_width / 2 - <<main>>.thickness
  expr: .Placement.Base.y = Sketch119.AttachmentOffset.Base.x
FEATURE [PartDesign::Pocket] Pocket074
  BaseFeature = -> Pocket036
  Direction = (0,0,-1)
  Length = 5
  Length2 = 5
  Midplane = true
  Profile = -> Binder036
  Type = 1
FEATURE [PartDesign::Mirrored] Mirrored
  MirrorPlane = -> YZ_Plane015
FEATURE [PartDesign::PolarPattern] PolarPattern015
  Angle = 360
  Axis = -> Z_Axis015
  Occurrences = 3
FEATURE [PartDesign::MultiTransform] MultiTransform
  BaseFeature = -> Pocket074
  Originals = -> [Pocket074]
  Transformations = -> [Mirrored,PolarPattern015]
FEATURE [Sketcher::SketchObject] Sketch120
  AttachmentOffset = pos=(0,-70,0) rot=(0,0,1;0rad)
  FullyConstrained = true
  MapMode = 5
  Placement = pos=(0,-70,0) rot=(0,0,1;0rad)
  Support = -> [XY_Plane016]
  sketch-geometry (1):
    g0: Circle CenterX=0 CenterY=0 CenterZ=0 NormalX=0 NormalY=0 NormalZ=1 AngleXU=0 Radius=4.25
  constraints (2):
    c: Coincident(g0,g-1)
    c: Diameter(g0) = 8.5
FEATURE [PartDesign::Pocket] Pocket087
  BaseFeature = -> MultiTransform
  Direction = (0,0,-1)
  Length = 5
  Length2 = 5
  Midplane = true
  Profile = -> Binder023
  Type = 1
FEATURE [PartDesign::PolarPattern] PolarPattern018
  Angle = 120
  Axis = -> Z_Axis015
  BaseFeature = -> Pocket087
  Occurrences = 2
  Originals = -> [Pocket087]
FEATURE [Sketcher::SketchObject] Sketch132
  FullyConstrained = true
  MapMode = 5
  Support = -> [XY_Plane016]
  expr: Constraints[1] = Sketch048.Constraints[1]
  sketch-geometry (3):
    g0: Circle CenterX=0 CenterY=0 CenterZ=0 NormalX=0 NormalY=0 NormalZ=1 AngleXU=0 Radius=212.348
    g1: Circle CenterX=0 CenterY=0 CenterZ=0 NormalX=0 NormalY=0 NormalZ=1 AngleXU=0 Radius=202.348
    g2: LineSegment StartX=202.348 StartY=0 StartZ=0 EndX=212.348 EndY=0 EndZ=0
  constraints (8):
    c: Coincident(g0,g-1)
    c: Radius(g0) = 212.348
    c: Coincident(g1,g0)
    c: PointOnObject(g2,g1)
    c: PointOnObject(g2,g0)
    c: Horizontal(g2)
    c: PointOnObject(g0,g2)
    c: DistanceX(g2,g2) = 10
FEATURE [PartDesign::Pad] Pad030
  BaseFeature = -> PolarPattern018
  Direction = (0,0,1)
  Length = 3
  Length2 = 10
  Profile = -> Sketch132
  ReferenceAxis = -> Sketch132 [N_Axis]
  Type = 0
  expr: Length = Pad013.Length
FEATURE [PartDesign::Body] Body001003005003  label="basement"
  Group = -> [Sketch048,Pad013,Sketch049,Binder004,DatumPlane017,Sketch050,Local_CS017,Sketch051,Binder005,DatumPlane018,Sketch057,Sketch058,Pocket027,Local_CS021,Local_CS022,DatumPlane019,DatumPlane020,Sketch061,Sketch062,Sketch063,Sketch064,Sketch075,Pocket036,Binder018,Binder023,Binder036,Pocket074,MultiTransform,Mirrored,PolarPattern015,Sketch120,Pocket087,PolarPattern018,Sketch132,Pad030]
  Origin = -> Origin015
  Tip = -> Pad030
COMPONENT P5 — recipe-attached ("Body001003005003003", modeled in this document).
Construction recipe (the document's own serialized feature program — sketch geometry with constraints, then the solid features built on it; lengths are millimeters unless a unit is written):

FEATURE [Sketcher::SketchObject] Sketch052
  FullyConstrained = true
  MapMode = 5
  Support = -> [XY_Plane017]
  expr: .Constraints.r = Sketch003.Constraints.max_r
  expr: Constraints[13] = 15mm + <<main>>.end_face_width / 2
  sketch-geometry (6):
    g0: ArcOfCircle CenterX=0 CenterY=0 CenterZ=0 NormalX=0 NormalY=0 NormalZ=1 AngleXU=0 Radius=199.848 StartAngle=0.699923 EndAngle=1.5708
    g1: ArcOfCircle CenterX=0 CenterY=0 CenterZ=0 NormalX=0 NormalY=0 NormalZ=1 AngleXU=0 Radius=209.848 StartAngle=0.699923 EndAngle=1.5708
    g2: ArcOfCircle CenterX=156.687 CenterY=131.955 CenterZ=0 NormalX=0 NormalY=0 NormalZ=1 AngleXU=0 Radius=5 StartAngle=3.84152 EndAngle=6.98311
    g3: LineSegment StartX=1.22e-14 StartY=199.848 StartZ=0 EndX=1.28e-14 EndY=209.848 EndZ=0
    g4: ArcOfCircle CenterX=0 CenterY=0 CenterZ=0 NormalX=0 NormalY=0 NormalZ=1 AngleXU=0 Radius=204.848 StartAngle=0.675514 EndAngle=1.5708
    g5: LineSegment StartX=0 StartY=0 StartZ=0 EndX=177.404 EndY=102.424 EndZ=0
  constraints (18):
    c: Coincident(g0,g-1)
    c: PointOnObject(g0,g-2)
    c: Coincident(g1,g0)
    c: PointOnObject(g1,g-2)
    c: Coincident(g3,g1)
    c: DistanceY(g1) = 209.848  'r'
    c: DistanceY(g0,g1) = 10  'width'
    c: Tangent(g2,g0) = 1.5708
    c: Tangent(g2,g1) = -1.5708
    c: Coincident(g4,g0)
    c: PointOnObject(g4,g2)
    c: Coincident(g5,g0)
    c: Angle(g-1,g5) = 0.523599
    c: Distance(g4,g5) = 31
    c: Coincident(g3,g0)
    c: PointOnObject(g2,g4)
    c: PointOnObject(g4,g-2)
    c: PointOnObject(g5,g4)
FEATURE [PartDesign::Pad] Pad014
  Direction = (0,0,1)
  Length = 3
  Length2 = 10
  Profile = -> Sketch052
  ReferenceAxis = -> Sketch052 [N_Axis]
  Type = 0
FEATURE [PartDesign::CoordinateSystem] Local_CS018
  AttacherType = Attacher::AttachEngine3D
  MapMode = 5
  Support = -> [XY_Plane017]
FEATURE [Sketcher::SketchObject] Sketch055
  FullyConstrained = true
  MapMode = 5
  Support = -> [XY_Plane017]
  expr: .Constraints.r = Sketch052.Constraints[5]
  expr: .Constraints.width = Sketch052.Constraints[6]
  expr: Constraints[12] = Sketch052.Constraints[12]
  expr: Constraints[13] = Sketch052.Constraints[13]
  expr: Constraints[25] = <<main>>.rivet_d
  sketch-geometry (9):
    g0: ArcOfCircle CenterX=0 CenterY=0 CenterZ=0 NormalX=0 NormalY=0 NormalZ=1 AngleXU=0 Radius=199.848 StartAngle=0.699923 EndAngle=1.5708
    g1: ArcOfCircle CenterX=0 CenterY=0 CenterZ=0 NormalX=0 NormalY=0 NormalZ=1 AngleXU=0 Radius=209.848 StartAngle=0.699923 EndAngle=1.5708
    g2: ArcOfCircle CenterX=156.687 CenterY=131.955 CenterZ=0 NormalX=0 NormalY=0 NormalZ=1 AngleXU=0 Radius=5 StartAngle=3.84152 EndAngle=6.98311
    g3: LineSegment StartX=1.22e-14 StartY=199.848 StartZ=0 EndX=1.28e-14 EndY=209.848 EndZ=0
    g4: ArcOfCircle CenterX=0 CenterY=0 CenterZ=0 NormalX=0 NormalY=0 NormalZ=1 AngleXU=0 Radius=204.848 StartAngle=0.675514 EndAngle=1.5708
    g5: LineSegment StartX=0 StartY=0 StartZ=0 EndX=177.404 EndY=102.424 EndZ=0
    g6: LineSegment StartX=1.22e-14 StartY=203.148 StartZ=0 EndX=1.31e-14 EndY=206.548 EndZ=0
    g7: ArcOfCircle CenterX=1.25e-14 CenterY=204.848 CenterZ=0 NormalX=0 NormalY=0 NormalZ=1 AngleXU=0 Radius=1.7 StartAngle=4.71239 EndAngle=7.85398
    g8: Circle CenterX=143.11 CenterY=146.569 CenterZ=0 NormalX=0 NormalY=0 NormalZ=1 AngleXU=0 Radius=1.7
  constraints (27):
    c: Coincident(g0,g-1)
    c: PointOnObject(g0,g-2)
    c: Coincident(g1,g0)
    c: PointOnObject(g1,g-2)
    c: Coincident(g3,g1)
    c: DistanceY(g1) = 209.848  'r'
    c: DistanceY(g0,g1) = 10  'width'
    c: Tangent(g2,g0) = 1.5708
    c: Tangent(g2,g1) = -1.5708
    c: Coincident(g4,g0)
    c: PointOnObject(g4,g2)
    c: Coincident(g5,g0)
    c: Angle(g-1,g5) = 0.523599
    c: Distance(g4,g5) = 31
    c: Coincident(g3,g0)
    c: PointOnObject(g2,g4)
    c: PointOnObject(g4,g-2)
    c: PointOnObject(g5,g4)
    c: PointOnObject(g6,g3)
    c: PointOnObject(g6,g3)
    c: Coincident(g7,g4)
    c: Coincident(g7,g6)
    c: Coincident(g7,g6)
    c: PointOnObject(g8,g4)
    c: Equal(g8,g7)
    c: Diameter(g7) = 3.4
    c: DistanceX(g8) = 143.11
FEATURE [PartDesign::Pocket] Pocket019
  BaseFeature = -> Pad014
  Direction = (0,0,-1)
  Length = 5
  Length2 = 5
  Midplane = true
  Profile = -> Sketch055
  ReferenceAxis = -> Sketch055 [N_Axis]
  Type = 1
FEATURE [PartDesign::Mirrored] Mirrored019
  BaseFeature = -> Pocket019
  MirrorPlane = -> Sketch052 [V_Axis]
  Originals = -> [Pad014,Pocket019]
FEATURE [PartDesign::Body] Body001003005003003
  Group = -> [Sketch052,Pad014,Pocket019,Mirrored019,Local_CS018,Sketch055]
  Origin = -> Origin016
  Tip = -> Mirrored019
COMPONENT P6 — recipe-attached ("basement2", modeled in this document).
Construction recipe (the document's own serialized feature program — sketch geometry with constraints, then the solid features built on it; lengths are millimeters unless a unit is written):

FEATURE [Sketcher::SketchObject] Sketch076
  FullyConstrained = true
  MapMode = 5
  Support = -> [XY_Plane025]
  expr: Constraints[1] = (180mm - 11.5mm) * 2
  sketch-geometry (1):
    g0: Circle CenterX=0 CenterY=0 CenterZ=0 NormalX=0 NormalY=0 NormalZ=1 AngleXU=0 Radius=168.5
  constraints (2):
    c: Coincident(g0,g-1)
    c: Diameter(g0) = 337
FEATURE [PartDesign::Pad] Pad020
  Direction = (0,0,1)
  Length = 3
  Length2 = 10
  Profile = -> Sketch076
  ReferenceAxis = -> Sketch076 [N_Axis]
  Type = 0
FEATURE [PartDesign::SubShapeBinder] Binder044
  BindCopyOnChange = 0
  BindMode = 0
  ClaimChildren = false
  Context = -> Body001003005003011 [Binder044.]
  Fuse = false
  MakeFace = true
  OffsetFill = false
  OffsetIntersection = false
  OffsetJoinType = 0
  OffsetOpenResult = false
  PartialLoad = false
  Relative = true
  Support = -> [Body001003005003[Pocket036.Sketch075.]]
  _Version = 2
FEATURE [PartDesign::SubShapeBinder] Binder045
  BindCopyOnChange = 0
  BindMode = 0
  ClaimChildren = false
  Context = -> Body001003005003011 [Binder045.]
  Fuse = false
  MakeFace = true
  OffsetFill = false
  OffsetIntersection = false
  OffsetJoinType = 0
  OffsetOpenResult = false
  PartialLoad = false
  Placement = pos=(0,0,0) rot=(0,0,1;0.785398rad)
  Relative = true
  Support = -> [Body001003005003[Pocket036.Sketch075.]]
  _Version = 2
FEATURE [PartDesign::Pocket] Pocket088
  BaseFeature = -> Pad020
  Direction = (0,0,-1)
  Length = 5
  Length2 = 5
  Midplane = true
  Profile = -> Binder044
  Type = 1
FEATURE [PartDesign::Hole] Hole
  BaseFeature = -> Pocket088
  CustomThreadClearance = 0
  Depth = 25
  DepthType = 0
  Diameter = 15.5
  DrillForDepth = false
  DrillPoint = 1
  DrillPointAngle = 118
  HoleCutCountersinkAngle = 90
  HoleCutCustomValues = false
  HoleCutDepth = 0
  HoleCutDiameter = 6.1
  HoleCutType = 0
  ModelThread = false
  Profile = -> Binder045
  Reversed = true
  Tapered = false
  TaperedAngle = 90
  ThreadClass = 0
  ThreadDepth = 25
  ThreadDepthType = 0
  ThreadDirection = 0
  ThreadFit = 0
  ThreadSize = 0
  ThreadType = 0
  Threaded = false
  UseCustomThreadClearance = false
FEATURE [PartDesign::Body] Body001003005003011  label="basement2"
  Group = -> [Sketch076,Pad020,Binder044,Binder045,Pocket088,Hole]
  Origin = -> Origin024
  Tip = -> Hole
COMPONENT P7 — recipe-attached ("Body001003005003012", modeled in this document).
Construction recipe (the document's own serialized feature program — sketch geometry with constraints, then the solid features built on it; lengths are millimeters unless a unit is written):

FEATURE [Sketcher::SketchObject] Sketch078
  FullyConstrained = true
  MapMode = 5
  Placement = pos=(0,0,0) rot=(1,0,0;1.5708rad)
  Support = -> [XZ_Plane025]
FEATURE [Sketcher::SketchObject] Sketch079
  FullyConstrained = true
  MapMode = 5
  Placement = pos=(0,0,0) rot=(0.57735,0.57735,0.57735;2.0944rad)
  Support = -> [YZ_Plane025]
  expr: Constraints[8] = <<main>>.basin_height
  sketch-geometry (3):
    g0: LineSegment StartX=15 StartY=0 StartZ=0 EndX=0 EndY=0 EndZ=0
    g1: LineSegment StartX=0 StartY=0 StartZ=0 EndX=0 EndY=157 EndZ=0
    g2: LineSegment StartX=0 StartY=157 StartZ=0 EndX=15 EndY=157 EndZ=0
  constraints (9):
    c: PointOnObject(g0,g-1)
    c: Coincident(g0,g-1)
    c: Coincident(g1,g0)
    c: PointOnObject(g1,g-2)
    c: Coincident(g2,g1)
    c: Horizontal(g2)
    c: DistanceX(g0,g0) = 15
    c: Vertical(g0,g2)
    c: DistanceY(g1) = 157
FEATURE [PartDesign::FeaturePython] BaseBend  # WARN: FeaturePython — macro-defined, semantics opaque (R4)
  BendSide = 0
  BendSketch = -> Sketch079
  MidPlane = true
  Reverse = false
  length = 15
  radius = 2
  thickness = 1
FEATURE [Sketcher::SketchObject] Sketch080
  AttachmentOffset = pos=(0,7.5,0) rot=(0,0,1;0rad)
  FullyConstrained = true
  MapMode = 5
  Placement = pos=(0,7.5,0) rot=(0,0,1;0rad)
  Support = -> [XY_Plane026]
  sketch-geometry (1):
    g0: Circle CenterX=0 CenterY=0 CenterZ=0 NormalX=0 NormalY=0 NormalZ=1 AngleXU=0 Radius=1.65
  constraints (3):
    c: PointOnObject(g0,g-2)
    c: Diameter(g0) = 3.3
    c: DistanceY(g0) = 0
FEATURE [PartDesign::Pocket] Pocket039
  BaseFeature = -> BaseBend
  Direction = (0,0,-1)
  Length = 5
  Length2 = 5
  Profile = -> Sketch080
  ReferenceAxis = -> Sketch080 [N_Axis]
  Reversed = true
  Type = 1
FEATURE [Sketcher::SketchObject] Sketch081
  FullyConstrained = true
  MapMode = 5
  Support = -> [XY_Plane026]
  sketch-geometry (3):
    g0: ArcOfCircle CenterX=4.5 CenterY=12 CenterZ=0 NormalX=0 NormalY=0 NormalZ=1 AngleXU=0 Radius=3 StartAngle=1e-16 EndAngle=1.57079
    g1: LineSegment StartX=4.50001 StartY=15 StartZ=0 EndX=7.5 EndY=15 EndZ=0
    g2: LineSegment StartX=7.5 StartY=12 StartZ=0 EndX=7.5 EndY=15 EndZ=0
  constraints (9):
    c: Diameter(g0) = 6
    c: Coincident(g1,g0)
    c: Tangent(g1,g0)
    c: Coincident(g2,g1)
    c: Vertical(g2)
    c: Horizontal(g1)
    c: DistanceX(g1) = 7.5
    c: DistanceY(g1) = 15
    c: Tangent(g2,g0) = -1.5708
FEATURE [PartDesign::Pocket] Pocket040
  BaseFeature = -> Pocket039
  Direction = (0,0,-1)
  Length = 5
  Length2 = 5
  Midplane = true
  Profile = -> Sketch081
  ReferenceAxis = -> Sketch081 [N_Axis]
  Type = 1
FEATURE [PartDesign::Mirrored] Mirrored028
  BaseFeature = -> Pocket040
  MirrorPlane = -> Sketch081 [V_Axis]
  Originals = -> [Pocket040]
FEATURE [PartDesign::Body] Body001003005003012
  Group = -> [Sketch078,Sketch079,BaseBend,Sketch080,Pocket039,Sketch081,Pocket040,Mirrored028]
  Origin = -> Origin025
  Tip = -> Mirrored028
COMPONENT P8 — recipe-attached ("plexiglass_holder_top", modeled in this document).
Construction recipe (the document's own serialized feature program — sketch geometry with constraints, then the solid features built on it; lengths are millimeters unless a unit is written):

FEATURE [Sketcher::SketchObject] Sketch082
  FullyConstrained = false
  MapMode = 5
  Support = -> [XY_Plane027]
  expr: Constraints[20] = <<main>>.end_face_width / 2 + 2mm
  expr: Constraints[2] = Sketch052.Constraints.r - Sketch052.Constraints.width - 2mm
  expr: Constraints[41] = <<main>>.end_face_width / 2
  sketch-geometry (19):
    g0: ArcOfCircle CenterX=0 CenterY=1.42e-14 CenterZ=0 NormalX=0 NormalY=0 NormalZ=1 AngleXU=0 Radius=197.848 StartAngle=0.657286 EndAngle=1.5708
    g1: LineSegment StartX=1.21e-14 StartY=197.848 StartZ=0 EndX=1.12e-14 EndY=182.848 EndZ=0
    g2: ArcOfCircle CenterX=0 CenterY=1.42e-14 CenterZ=0 NormalX=0 NormalY=0 NormalZ=1 AngleXU=0 Radius=182.848 StartAngle=0.657286 EndAngle=1.5708
    g3: ArcOfCircle CenterX=150.69 CenterY=116.297 CenterZ=0 NormalX=0 NormalY=0 NormalZ=1 AngleXU=0 Radius=7.5 StartAngle=3.79888 EndAngle=6.94047
    g4: LineSegment StartX=0 StartY=1.42e-14 StartZ=0 EndX=165.582 EndY=95.5988 EndZ=0
    g5: GeomPoint X=155.154 Y=110.271 Z=0
    g6: LineSegment StartX=165.582 StartY=95.5988 StartZ=0 EndX=155.154 EndY=110.271 EndZ=0
    g7: ArcOfCircle CenterX=0 CenterY=1.42e-14 CenterZ=0 NormalX=0 NormalY=0 NormalZ=1 AngleXU=0 Radius=190.348 StartAngle=0.617882 EndAngle=1.5708
    g8: ArcOfCircle CenterX=0 CenterY=1.42e-14 CenterZ=0 NormalX=0 NormalY=0 NormalZ=1 AngleXU=0 Radius=190.348 StartAngle=0.641212 EndAngle=1.5708
    g9: ArcOfCircle CenterX=0 CenterY=1.42e-14 CenterZ=0 NormalX=0 NormalY=0 NormalZ=1 AngleXU=0 Radius=197.848 StartAngle=0.619862 EndAngle=0.657286
    g10: LineSegment StartX=155.154 StartY=110.271 StartZ=0 EndX=160.726 EndY=113.488 EndZ=0
    g11: ArcOfCircle CenterX=160.226 CenterY=114.354 CenterZ=0 NormalX=0 NormalY=0 NormalZ=1 AngleXU=0 Radius=1 StartAngle=5.23599 EndAngle=6.90305
    g12: ArcOfCircle CenterX=0 CenterY=1.42e-14 CenterZ=0 NormalX=0 NormalY=0 NormalZ=1 AngleXU=0 Radius=182.848 StartAngle=0.626692 EndAngle=0.657286
    g13: LineSegment StartX=155.154 StartY=110.271 StartZ=0 EndX=149.412 EndY=106.955 EndZ=0
    g14: ArcOfCircle CenterX=148.912 CenterY=107.821 CenterZ=0 NormalX=0 NormalY=0 NormalZ=1 AngleXU=0 Radius=1 StartAngle=3.76829 EndAngle=5.23599
    g15: ArcOfCircle CenterX=0 CenterY=1.42e-14 CenterZ=0 NormalX=0 NormalY=0 NormalZ=1 AngleXU=0 Radius=197.848 StartAngle=0.604557 EndAngle=1.5708
    g16: LineSegment StartX=162.781 StartY=112.457 StartZ=0 EndX=0 EndY=1.42e-14 EndZ=0
    g17: LineSegment StartX=162.781 StartY=112.457 StartZ=0 EndX=0 EndY=112.457 EndZ=0
    g18: LineSegment StartX=0 StartY=1.42e-14 StartZ=0 EndX=162.781 EndY=112.457 EndZ=0
  constraints (52):
    c: Coincident(g0,g-1)
    c: PointOnObject(g0,g-2)
    c: DistanceY(g0) = 197.848
    c: Coincident(g1,g0)
    c: PointOnObject(g1,g-2)
    c: Coincident(g2,g0)
    c: Coincident(g2,g1)
    c: Tangent(g3,g0) = -1.5708
    c: Tangent(g3,g2) = 1.5708
    c: DistanceY(g1,g1) = 15
    c: Coincident(g4,g0)
    c: Angle(g-1,g4) = 0.523599
    c: PointOnObject(g5,g3)
    c: Coincident(g6,g4)
    c: Coincident(g6,g5)
    c: Coincident(g7,g0)
    c: Coincident(g7,g5)
    c: PointOnObject(g7,g1)
    c: PointOnObject(g3,g7)
    c: Tangent(g6,g7)
    c: Distance(g6) = 18
    c: Coincident(g8,g0)
    c: PointOnObject(g8,g-2)
    c: DistanceY(g8,g0) = 7.5
    c: Coincident(g9,g0)
    c: Coincident(g9,g0)
    c: Coincident(g10,g5)
    c: Parallel(g10,g4)
    c: Tangent(g9,g11) = -1.5708
    c: Tangent(g10,g11) = -1.5708
    c: Diameter(g11) = 2
    c: Coincident(g12,g0)
    c: Coincident(g12,g2)
    c: Coincident(g13,g10)
    c: Parallel(g13,g10)
    c: Tangent(g12,g14) = 1.5708
    c: Tangent(g13,g14) = 1.5708
    c: Equal(g14,g11)
    c: Coincident(g15,g0)
    c: PointOnObject(g15,g-2)
    c: Equal(g15,g9)
    c: Distance(g15,g4) = 16
    c: Coincident(g16,g15)
    c: Coincident(g16,g0)
    c: Angle(g16,g-2) = 0.966239
    c: Coincident(g17,g15)
    c: PointOnObject(g17,g-2)
    c: Horizontal(g17)
    c: DistanceX(g17,g17) = 162.781
    c: Coincident(g18,g0)
    c: Coincident(g18,g15)
    c: Angle(g16,g-2) = 0.966239
FEATURE [PartDesign::Pad] Pad021
  Direction = (0,0,1)
  Length = 3
  Length2 = 10
  Profile = -> Sketch082
  ReferenceAxis = -> Sketch082 [N_Axis]
  Type = 0
FEATURE [Sketcher::SketchObject] Sketch083
  FullyConstrained = true
  MapMode = 5
  Support = -> [XY_Plane027]
  expr: Constraints[11] = Sketch082.Constraints[11]
  expr: Constraints[20] = Sketch082.Constraints[20]
  expr: Constraints[23] = Sketch082.Constraints[23]
  expr: Constraints[25] = <<main>>.rivet_d
  expr: Constraints[2] = Sketch082.Constraints[2]
  expr: Constraints[9] = Sketch082.Constraints[9]
  sketch-geometry (11):
    g0: ArcOfCircle CenterX=0 CenterY=0 CenterZ=0 NormalX=0 NormalY=0 NormalZ=1 AngleXU=0 Radius=197.848 StartAngle=0.657286 EndAngle=1.5708
    g1: LineSegment StartX=1.21e-14 StartY=197.848 StartZ=0 EndX=1.12e-14 EndY=182.848 EndZ=0
    g2: ArcOfCircle CenterX=0 CenterY=0 CenterZ=0 NormalX=0 NormalY=0 NormalZ=1 AngleXU=0 Radius=182.848 StartAngle=0.657286 EndAngle=1.5708
    g3: ArcOfCircle CenterX=150.69 CenterY=116.297 CenterZ=0 NormalX=0 NormalY=0 NormalZ=1 AngleXU=0 Radius=7.5 StartAngle=3.79888 EndAngle=6.94047
    g4: LineSegment StartX=0 StartY=0 StartZ=0 EndX=165.582 EndY=95.5988 EndZ=0
    g5: GeomPoint X=155.154 Y=110.271 Z=0
    g6: LineSegment StartX=165.582 StartY=95.5988 StartZ=0 EndX=155.154 EndY=110.271 EndZ=0
    g7: ArcOfCircle CenterX=0 CenterY=0 CenterZ=0 NormalX=0 NormalY=0 NormalZ=1 AngleXU=0 Radius=190.348 StartAngle=0.617882 EndAngle=1.5708
    g8: ArcOfCircle CenterX=0 CenterY=0 CenterZ=0 NormalX=0 NormalY=0 NormalZ=1 AngleXU=0 Radius=190.348 StartAngle=0.670423 EndAngle=1.5708
    g9: Circle CenterX=149.149 CenterY=118.267 CenterZ=0 NormalX=0 NormalY=0 NormalZ=1 AngleXU=0 Radius=1.7
    g10: Circle CenterX=-149.149 CenterY=118.267 CenterZ=0 NormalX=0 NormalY=0 NormalZ=1 AngleXU=0 Radius=1.7
  constraints (29):
    c: Coincident(g0,g-1)
    c: PointOnObject(g0,g-2)
    c: DistanceY(g0) = 197.848
    c: Coincident(g1,g0)
    c: PointOnObject(g1,g-2)
    c: Coincident(g2,g0)
    c: Coincident(g2,g1)
    c: Tangent(g3,g0) = -1.5708
    c: Tangent(g3,g2) = 1.5708
    c: DistanceY(g1,g1) = 15
    c: Coincident(g4,g0)
    c: Angle(g-1,g4) = 0.523599
    c: PointOnObject(g5,g3)
    c: Coincident(g6,g4)
    c: Coincident(g6,g5)
    c: Coincident(g7,g0)
    c: Coincident(g7,g5)
    c: PointOnObject(g7,g1)
    c: PointOnObject(g3,g7)
    c: Tangent(g6,g7)
    c: Distance(g6) = 18
    c: Coincident(g8,g0)
    c: PointOnObject(g8,g-2)
    c: DistanceY(g8,g0) = 7.5
    c: Coincident(g9,g8)
    c: Diameter(g9) = 3.4
    c: Symmetric(g10,g9,g-2)
    c: Equal(g10,g9)
    c: Distance(g5,g9) = 10
FEATURE [PartDesign::Mirrored] Mirrored029
  BaseFeature = -> Pad021
  MirrorPlane = -> Sketch082 [V_Axis]
  Originals = -> [Pad021]
  Refine = true
FEATURE [PartDesign::Pocket] Pocket041
  BaseFeature = -> Mirrored029
  Direction = (0,0,-1)
  Length = 5
  Length2 = 5
  Midplane = true
  Profile = -> Sketch083
  ReferenceAxis = -> Sketch083 [N_Axis]
  Type = 1
FEATURE [Sketcher::SketchObject] Sketch084
  FullyConstrained = true
  MapMode = 5
  Support = -> [XY_Plane027]
  expr: Constraints[11] = Sketch082.Constraints[11]
  expr: Constraints[20] = Sketch082.Constraints[20]
  expr: Constraints[27] = Sketch082.Constraints[30]
  expr: Constraints[2] = Sketch082.Constraints[2]
  expr: Constraints[36] = <<main>>.rivet_d
  expr: Constraints[9] = Sketch082.Constraints[9]
  sketch-geometry (15):
    g0: ArcOfCircle CenterX=0 CenterY=0 CenterZ=0 NormalX=0 NormalY=0 NormalZ=1 AngleXU=0 Radius=197.848 StartAngle=0.657286 EndAngle=1.5708
    g1: LineSegment StartX=1.21e-14 StartY=197.848 StartZ=0 EndX=1.12e-14 EndY=182.848 EndZ=0
    g2: ArcOfCircle CenterX=0 CenterY=0 CenterZ=0 NormalX=0 NormalY=0 NormalZ=1 AngleXU=0 Radius=182.848 StartAngle=0.657286 EndAngle=1.5708
    g3: ArcOfCircle CenterX=150.69 CenterY=116.297 CenterZ=0 NormalX=0 NormalY=0 NormalZ=1 AngleXU=0 Radius=7.5 StartAngle=3.79888 EndAngle=6.94047
    g4: LineSegment StartX=0 StartY=0 StartZ=0 EndX=165.582 EndY=95.5988 EndZ=0
    g5: GeomPoint X=155.154 Y=110.271 Z=0
    g6: LineSegment StartX=165.582 StartY=95.5988 StartZ=0 EndX=155.154 EndY=110.271 EndZ=0
    g7: ArcOfCircle CenterX=0 CenterY=0 CenterZ=0 NormalX=0 NormalY=0 NormalZ=1 AngleXU=0 Radius=190.348 StartAngle=0.617882 EndAngle=1.5708
    g8: ArcOfCircle CenterX=0 CenterY=0 CenterZ=0 NormalX=0 NormalY=0 NormalZ=1 AngleXU=0 Radius=197.848 StartAngle=0.619862 EndAngle=0.657286
    g9: LineSegment StartX=155.154 StartY=110.271 StartZ=0 EndX=160.726 EndY=113.488 EndZ=0
    g10: ArcOfCircle CenterX=160.226 CenterY=114.354 CenterZ=0 NormalX=0 NormalY=0 NormalZ=1 AngleXU=0 Radius=1 StartAngle=5.23599 EndAngle=6.90305
    g11: ArcOfCircle CenterX=0 CenterY=0 CenterZ=0 NormalX=0 NormalY=0 NormalZ=1 AngleXU=0 Radius=182.848 StartAngle=0.626692 EndAngle=0.657286
    g12: LineSegment StartX=155.154 StartY=110.271 StartZ=0 EndX=149.412 EndY=106.955 EndZ=0
    g13: ArcOfCircle CenterX=148.912 CenterY=107.821 CenterZ=0 NormalX=0 NormalY=0 NormalZ=1 AngleXU=0 Radius=1 StartAngle=3.76829 EndAngle=5.23599
    g14: Circle CenterX=1.17e-14 CenterY=190.348 CenterZ=0 NormalX=0 NormalY=0 NormalZ=1 AngleXU=0 Radius=1.7
  constraints (37):
    c: Coincident(g0,g-1)
    c: PointOnObject(g0,g-2)
    c: DistanceY(g0) = 197.848
    c: Coincident(g1,g0)
    c: PointOnObject(g1,g-2)
    c: Coincident(g2,g0)
    c: Coincident(g2,g1)
    c: Tangent(g3,g0) = -1.5708
    c: Tangent(g3,g2) = 1.5708
    c: DistanceY(g1,g1) = 15
    c: Coincident(g4,g0)
    c: Angle(g-1,g4) = 0.523599
    c: PointOnObject(g5,g3)
    c: Coincident(g6,g4)
    c: Coincident(g6,g5)
    c: Coincident(g7,g0)
    c: Coincident(g7,g5)
    c: PointOnObject(g7,g1)
    c: PointOnObject(g3,g7)
    c: Tangent(g6,g7)
    c: Distance(g6) = 18
    c: Coincident(g8,g0)
    c: Coincident(g8,g0)
    c: Coincident(g9,g5)
    c: Parallel(g9,g4)
    c: Tangent(g8,g10) = -1.5708
    c: Tangent(g9,g10) = -1.5708
    c: Diameter(g10) = 2
    c: Coincident(g11,g0)
    c: Coincident(g11,g2)
    c: Coincident(g12,g9)
    c: Parallel(g12,g9)
    c: Tangent(g11,g13) = 1.5708
    c: Tangent(g12,g13) = 1.5708
    c: Equal(g13,g10)
    c: Coincident(g14,g7)
    c: Diameter(g14) = 3.4
FEATURE [PartDesign::Pocket] Pocket042
  BaseFeature = -> Pocket041
  Direction = (0,0,-1)
  Length = 5
  Length2 = 5
  Midplane = true
  Profile = -> Sketch084
  ReferenceAxis = -> Sketch084 [N_Axis]
  Type = 1
FEATURE [PartDesign::Body] Body001003005003013  label="plexiglass_holder_top"
  Group = -> [Sketch082,Pad021,Sketch083,Mirrored029,Pocket041,Sketch084,Pocket042]
  Origin = -> Origin026
  Placement = pos=(0,0,0) rot=(0,0,1;1.0472rad)
  Tip = -> Pocket042
COMPONENT P9 — recipe-attached ("corner_72x15_material_0.30ansi", modeled in this document).
Construction recipe (the document's own serialized feature program — sketch geometry with constraints, then the solid features built on it; lengths are millimeters unless a unit is written):

FEATURE [Sketcher::SketchObject] Sketch085
  FullyConstrained = true
  MapMode = 5
  Placement = pos=(0,0,0) rot=(0.57735,0.57735,0.57735;2.0944rad)
  Support = -> [YZ_Plane028]
  sketch-geometry (2):
    g0: LineSegment StartX=0 StartY=23 StartZ=0 EndX=0 EndY=0 EndZ=0
    g1: LineSegment StartX=0 StartY=0 StartZ=0 EndX=23 EndY=0 EndZ=0
  constraints (6):
    c: PointOnObject(g0,g-2)
    c: Coincident(g0,g-1)
    c: Coincident(g1,g0)
    c: PointOnObject(g1,g-1)
    c: Equal(g1,g0)
    c: DistanceX(g1,g1) = 23  'length'
FEATURE [PartDesign::FeaturePython] BaseBend002  # WARN: FeaturePython — macro-defined, semantics opaque (R4)
  BendSide = 0
  BendSketch = -> Sketch085
  MidPlane = true
  Reverse = false
  length = 86
  radius = 2
  thickness = 0.5
FEATURE [Sketcher::SketchObject] Sketch086
  AttachmentOffset = pos=(43,23,0) rot=(0,0,1;0rad)
  FullyConstrained = true
  MapMode = 5
  Placement = pos=(43,23,0) rot=(0,0,1;0rad)
  Support = -> [XY_Plane029]
  expr: .AttachmentOffset.Base.x = BaseBend002.length / 2
  expr: .AttachmentOffset.Base.y = Sketch085.Constraints.length
  sketch-geometry (3):
    g0: ArcOfCircle CenterX=-7.5 CenterY=-7.5 CenterZ=0 NormalX=0 NormalY=0 NormalZ=1 AngleXU=0 Radius=7.5 StartAngle=0 EndAngle=1.5708
    g1: LineSegment StartX=0 StartY=-7.5 StartZ=0 EndX=0 EndY=0 EndZ=0
    g2: LineSegment StartX=0 StartY=0 StartZ=0 EndX=-7.50003 EndY=-6.21876e-11 EndZ=0
  constraints (8):
    c: PointOnObject(g0,g-2)
    c: PointOnObject(g0,g-1)
    c: Coincident(g1,g-1)
    c: Coincident(g2,g1)
    c: Coincident(g2,g0)
    c: Tangent(g2,g0)
    c: Tangent(g1,g0) = -1.5708
    c: Diameter(g0) = 15
FEATURE [PartDesign::Pocket] Pocket047
  BaseFeature = -> BaseBend002
  Direction = (0,0,-1)
  Length = 5
  Length2 = 5
  Midplane = true
  Profile = -> Sketch086
  ReferenceAxis = -> Sketch086 [N_Axis]
  Type = 1
FEATURE [PartDesign::Mirrored] Mirrored032
  MirrorPlane = -> YZ_Plane028
FEATURE [PartDesign::PolarPattern] PolarPattern010
  Angle = 90
  Axis = -> X_Axis028
  Occurrences = 2
FEATURE [PartDesign::MultiTransform] MultiTransform011
  BaseFeature = -> Pocket047
  Originals = -> [Pocket047]
  Transformations = -> [Mirrored032,PolarPattern010]
FEATURE [Sketcher::SketchObject] Sketch087
  AttachmentOffset = pos=(0,14.5,0) rot=(0,0,1;0rad)
  FullyConstrained = true
  MapMode = 5
  Placement = pos=(0,14.5,0) rot=(0,0,1;0rad)
  Support = -> [XY_Plane029]
  expr: .AttachmentOffset.Base.y = 14.5mm
  expr: Constraints[3] = <<main>>.rivet_d
  sketch-geometry (2):
    g0: Circle CenterX=36 CenterY=0 CenterZ=0 NormalX=0 NormalY=0 NormalZ=1 AngleXU=0 Radius=1.7
    g1: Circle CenterX=-36 CenterY=0 CenterZ=0 NormalX=0 NormalY=0 NormalZ=1 AngleXU=0 Radius=1.7
  constraints (5):
    c: PointOnObject(g0,g-1)
    c: Symmetric(g1,g0,g-1)
    c: Equal(g0,g1)
    c: Diameter(g0) = 3.4
    c: DistanceX(g1,g0) = 72
FEATURE [PartDesign::Pocket] Pocket048
  BaseFeature = -> MultiTransform011
  Direction = (0,0,-1)
  Length = 5
  Length2 = 5
  Midplane = true
  Profile = -> Sketch087
  ReferenceAxis = -> Sketch087 [N_Axis]
  Type = 1
FEATURE [PartDesign::PolarPattern] PolarPattern011
  Angle = 90
  Axis = -> X_Axis028
  BaseFeature = -> Pocket048
  Occurrences = 2
  Originals = -> [Pocket048]
FEATURE [PartDesign::CoordinateSystem] Local_CS031
  AttacherType = Attacher::AttachEngine3D
  MapMode = 2
  Placement = pos=(0,14.5,0) rot=(0,0,1;0rad)
  Support = -> [Sketch087]
FEATURE [PartDesign::Body] Body001003005003015  label="corner_72x15_material_0.30ansi"
  Group = -> [Sketch085,BaseBend002,Sketch086,Pocket047,MultiTransform011,Mirrored032,PolarPattern010,Sketch087,Pocket048,PolarPattern011,Local_CS031]
  Origin = -> Origin028
  Tip = -> PolarPattern011
COMPONENT P10 — recipe-attached ("corner_5.5_material_0.30ansi", modeled in this document).
Construction recipe (the document's own serialized feature program — sketch geometry with constraints, then the solid features built on it; lengths are millimeters unless a unit is written):

FEATURE [PartDesign::Mirrored] Mirrored039
  MirrorPlane = -> YZ_Plane036
FEATURE [PartDesign::PolarPattern] PolarPattern014
  Angle = 90
  Axis = -> X_Axis036
  Occurrences = 2
FEATURE [Sketcher::SketchObject] Sketch108
  FullyConstrained = true
  MapMode = 5
  Placement = pos=(0,0,0) rot=(0.57735,0.57735,0.57735;2.0944rad)
  Support = -> [YZ_Plane036]
  sketch-geometry (2):
    g0: LineSegment StartX=0 StartY=23 StartZ=0 EndX=0 EndY=0 EndZ=0
    g1: LineSegment StartX=0 StartY=0 StartZ=0 EndX=23 EndY=0 EndZ=0
  constraints (6):
    c: PointOnObject(g0,g-2)
    c: Coincident(g0,g-1)
    c: Coincident(g1,g0)
    c: PointOnObject(g1,g-1)
    c: Equal(g1,g0)
    c: DistanceX(g1,g1) = 23  'length'
FEATURE [PartDesign::FeaturePython] BaseBend007  # WARN: FeaturePython — macro-defined, semantics opaque (R4)
  BendSide = 0
  BendSketch = -> Sketch108
  MidPlane = true
  Reverse = false
  length = 86
  radius = 2
  thickness = 0.5
FEATURE [Sketcher::SketchObject] Sketch109
  AttachmentOffset = pos=(43,23,0) rot=(0,0,1;0rad)
  FullyConstrained = true
  MapMode = 5
  Placement = pos=(43,23,0) rot=(0,0,1;0rad)
  Support = -> [XY_Plane037]
  expr: .AttachmentOffset.Base.x = BaseBend007.length / 2
  expr: .AttachmentOffset.Base.y = Sketch108.Constraints.length
  sketch-geometry (3):
    g0: ArcOfCircle CenterX=-7.5 CenterY=-7.5 CenterZ=0 NormalX=0 NormalY=0 NormalZ=1 AngleXU=0 Radius=7.5 StartAngle=0 EndAngle=1.5708
    g1: LineSegment StartX=0 StartY=-7.5 StartZ=0 EndX=0 EndY=0 EndZ=0
    g2: LineSegment StartX=0 StartY=0 StartZ=0 EndX=-7.50003 EndY=-6.21876e-11 EndZ=0
  constraints (8):
    c: PointOnObject(g0,g-2)
    c: PointOnObject(g0,g-1)
    c: Coincident(g1,g-1)
    c: Coincident(g2,g1)
    c: Coincident(g2,g0)
    c: Tangent(g2,g0)
    c: Tangent(g1,g0) = -1.5708
    c: Diameter(g0) = 15
FEATURE [PartDesign::Pocket] Pocket063
  BaseFeature = -> BaseBend007
  Direction = (0,0,-1)
  Length = 5
  Length2 = 5
  Midplane = true
  Profile = -> Sketch109
  ReferenceAxis = -> Sketch109 [N_Axis]
  Type = 1
FEATURE [PartDesign::MultiTransform] MultiTransform013
  BaseFeature = -> Pocket063
  Originals = -> [Pocket063]
  Transformations = -> [Mirrored039,PolarPattern014]
FEATURE [Sketcher::SketchObject] Sketch110
  AttachmentOffset = pos=(0,14.5,0) rot=(0,0,1;0rad)
  FullyConstrained = true
  MapMode = 5
  Placement = pos=(0,-3.2e-15,14.5) rot=(1,0,0;1.5708rad)
  Support = -> [XZ_Plane036]
  expr: .AttachmentOffset.Base.y = 14.5mm
  expr: Constraints[3] = <<main>>.rivet_d
  sketch-geometry (2):
    g0: Circle CenterX=36 CenterY=0 CenterZ=0 NormalX=0 NormalY=0 NormalZ=1 AngleXU=0 Radius=1.7
    g1: Circle CenterX=-36 CenterY=0 CenterZ=0 NormalX=0 NormalY=0 NormalZ=1 AngleXU=0 Radius=1.7
  constraints (5):
    c: PointOnObject(g0,g-1)
    c: Symmetric(g1,g0,g-1)
    c: Equal(g0,g1)
    c: Diameter(g0) = 3.4
    c: DistanceX(g1,g0) = 72
FEATURE [PartDesign::CoordinateSystem] Local_CS034
  AttacherType = Attacher::AttachEngine3D
  MapMode = 2
  Placement = pos=(0,-3.2e-15,14.5) rot=(1,0,0;1.5708rad)
  Support = -> [Sketch110]
FEATURE [PartDesign::Pocket] Pocket064
  BaseFeature = -> MultiTransform013
  Direction = (0,1,2e-16)
  Length = 5
  Length2 = 5
  Midplane = true
  Profile = -> Sketch110
  ReferenceAxis = -> Sketch110 [N_Axis]
  Type = 1
FEATURE [Sketcher::SketchObject] Sketch111
  AttachmentOffset = pos=(0,14.5,0) rot=(0,0,1;0rad)
  FullyConstrained = true
  MapMode = 5
  Placement = pos=(0,14.5,0) rot=(0,0,1;0rad)
  Support = -> [XY_Plane037]
  expr: .AttachmentOffset.Base.y = Sketch110.AttachmentOffset.Base.y
  expr: Constraints[3] = 5.5
  expr: Constraints[4] = Sketch110.Constraints[4]
  sketch-geometry (2):
    g0: Circle CenterX=36 CenterY=0 CenterZ=0 NormalX=0 NormalY=0 NormalZ=1 AngleXU=0 Radius=2.75
    g1: Circle CenterX=-36 CenterY=0 CenterZ=0 NormalX=0 NormalY=0 NormalZ=1 AngleXU=0 Radius=2.75
  constraints (5):
    c: PointOnObject(g0,g-1)
    c: Symmetric(g1,g0,g-1)
    c: Equal(g0,g1)
    c: Diameter(g0) = 5.5
    c: DistanceX(g1,g0) = 72
FEATURE [PartDesign::Pocket] Pocket065
  BaseFeature = -> Pocket064
  Direction = (0,0,-1)
  Length = 5
  Length2 = 5
  Midplane = true
  Profile = -> Sketch111
  ReferenceAxis = -> Sketch111 [N_Axis]
  Type = 1
FEATURE [PartDesign::Body] Body001003005003015002  label="corner_5.5_material_0.30ansi"
  Group = -> [Sketch108,BaseBend007,Sketch109,Pocket063,MultiTransform013,Mirrored039,PolarPattern014,Sketch110,Pocket064,Local_CS034,Sketch111,Pocket065]
  Origin = -> Origin036
  Tip = -> Pocket065
COMPONENT P11 — recipe-attached ("Body001003005003015005", modeled in this document).
Construction recipe (the document's own serialized feature program — sketch geometry with constraints, then the solid features built on it; lengths are millimeters unless a unit is written):

FEATURE [Sketcher::SketchObject] Sketch131
  FullyConstrained = true
  MapMode = 5
  Support = -> [XY_Plane042]
  sketch-geometry (5):
    g0: LineSegment StartX=-20 StartY=20 StartZ=0 EndX=-20 EndY=0 EndZ=0
    g1: LineSegment StartX=-20 StartY=0 StartZ=0 EndX=20 EndY=0 EndZ=0
    g2: LineSegment StartX=20 StartY=0 StartZ=0 EndX=20 EndY=20 EndZ=0
    g3: LineSegment StartX=20 StartY=20 StartZ=0 EndX=-20 EndY=20 EndZ=0
    g4: GeomPoint X=0 Y=10 Z=0
  constraints (13):
    c: Coincident(g0,g1)
    c: Coincident(g1,g2)
    c: Coincident(g2,g3)
    c: Coincident(g3,g0)
    c: Horizontal(g1)
    c: Horizontal(g3)
    c: Vertical(g0)
    c: Vertical(g2)
    c: Symmetric(g1,g0,g4)
    c: PointOnObject(g4,g-2)
    c: PointOnObject(g1,g-1)
    c: DistanceX(g1,g1) = 40
    c: DistanceY(g2) = 20
FEATURE [PartDesign::Pad] Pad029
  Direction = (0,0,1)
  Length = 1.5
  Length2 = 10
  Profile = -> Sketch131
  ReferenceAxis = -> Sketch131 [N_Axis]
  Type = 0
FEATURE [PartDesign::Body] Body001003005003015005
  Group = -> [Sketch131,Pad029]
  Origin = -> Origin041
  Tip = -> Pad029
COMPONENT P12 — recipe-attached ("Unfold_main", modeled in this document).
Construction recipe (the document's own serialized feature program — sketch geometry with constraints, then the solid features built on it; lengths are millimeters unless a unit is written):

FEATURE [PartDesign::FeatureBase] BaseFeature001
  BaseFeature = -> Unfold011
  Placement = pos=(0,0,208.372) rot=(0.57735,0.57735,-0.57735;4.18879rad)
  expr: Placement = <<Unfold>>.Placement
FEATURE [PartDesign::Pad] Pad031
  BaseFeature = -> BaseFeature001
  Direction = (-3e-16,5e-16,1)
  Length = 2.7
  Length2 = 10
  Placement = pos=(0,0,208.372) rot=(0.57735,0.57735,-0.57735;4.18879rad)
  Profile = -> BaseFeature001 [Face543]
  Type = 0
FEATURE [PartDesign::Body] Body001003005003015006  label="Unfold_main"
  BaseFeature = -> Unfold011
  Group = -> [BaseFeature001,Pad031]
  Origin = -> Origin042
  Tip = -> Pad031
COMPONENT P13 — recipe-attached ("Unfold_top", modeled in this document).
Construction recipe (the document's own serialized feature program — sketch geometry with constraints, then the solid features built on it; lengths are millimeters unless a unit is written):

FEATURE [PartDesign::FeatureBase] BaseFeature002
  BaseFeature = -> Unfold014
  Placement = pos=(0,0,0) rot=(0.707107,0.707107,0;3.14159rad)
  expr: Placement = Unfold014.Placement
FEATURE [PartDesign::Pad] Pad032
  BaseFeature = -> BaseFeature002
  Direction = (0,2e-16,1)
  Length = 2.7
  Length2 = 10
  Placement = pos=(0,0,0) rot=(0.707107,0.707107,0;3.14159rad)
  Profile = -> BaseFeature002 [Face2]
  Type = 0
FEATURE [PartDesign::Body] Body001003005003015007  label="Unfold_top"
  BaseFeature = -> Unfold014
  Group = -> [BaseFeature002,Pad032]
  Origin = -> Origin043
  Tip = -> Pad032
COMPONENT P14 — recipe-attached ("top_material_0.50ansi", modeled in this document).
Construction recipe (the document's own serialized feature program — sketch geometry with constraints, then the solid features built on it; lengths are millimeters unless a unit is written):

FEATURE [PartDesign::CoordinateSystem] LCS_0
  AttacherType = Attacher::AttachEngine3D
  MapMode = 2
  Support = -> [X_Axis029]
FEATURE [Sketcher::SketchObject] Sketch089
  FullyConstrained = true
  MapMode = 5
  Placement = pos=(0,0,0) rot=(1,0,0;1.5708rad)
  Support = -> [XZ_Plane029]
  sketch-geometry (5):
    g0: LineSegment StartX=-41.5 StartY=-36.5 StartZ=0 EndX=-41.5 EndY=0 EndZ=0
    g1: LineSegment StartX=-41.5 StartY=0 StartZ=0 EndX=41.5 EndY=0 EndZ=0
    g2: LineSegment StartX=41.5 StartY=0 StartZ=0 EndX=41.5 EndY=-36.5 EndZ=0
    g3: LineSegment StartX=41.5 StartY=-36.5 StartZ=0 EndX=-41.5 EndY=-36.5 EndZ=0
    g4: GeomPoint X=0 Y=-18.25 Z=0
  constraints (13):
    c: Coincident(g0,g1)
    c: Coincident(g1,g2)
    c: Coincident(g2,g3)
    c: Coincident(g3,g0)
    c: Horizontal(g1)
    c: Horizontal(g3)
    c: Vertical(g0)
    c: Vertical(g2)
    c: Symmetric(g1,g0,g4)
    c: PointOnObject(g4,g-2)
    c: PointOnObject(g1,g-1)
    c: DistanceX(g1,g1) = 83  'width'
    c: DistanceY(g2,g2) = 36.5
FEATURE [PartDesign::FeaturePython] BaseBend003  # WARN: FeaturePython — macro-defined, semantics opaque (R4)
  BendSide = 0
  BendSketch = -> Sketch089
  MidPlane = true
  Reverse = false
  length = 108.4
  radius = 0.01
  thickness = 0.3
  expr: radius = <<main>>.bend_r
FEATURE [Sketcher::SketchObject] Sketch090
  FullyConstrained = true
  MapMode = 5
  Support = -> [XY_Plane030]
  expr: Constraints[6] = <<main>>.end_face_width / 2
  sketch-geometry (6):
    g0: LineSegment StartX=0 StartY=-100 StartZ=0 EndX=14.5 EndY=-100 EndZ=0
    g1: LineSegment StartX=16 StartY=-98.5 StartZ=0 EndX=16 EndY=100 EndZ=0
    g2: LineSegment StartX=16 StartY=100 StartZ=0 EndX=0 EndY=109.238 EndZ=0
    g3: LineSegment StartX=0 StartY=109.238 StartZ=0 EndX=0 EndY=-100 EndZ=0
    g4: ArcOfCircle CenterX=14.5 CenterY=-98.5 CenterZ=0 NormalX=0 NormalY=0 NormalZ=1 AngleXU=0 Radius=1.5 StartAngle=4.71239 EndAngle=6.28319
    g5: GeomPoint X=16 Y=-100 Z=0
  constraints (15):
    c: Coincident(g1,g2)
    c: Coincident(g2,g3)
    c: Coincident(g3,g0)
    c: Horizontal(g0)
    c: Vertical(g3)
    c: PointOnObject(g0,g-2)
    c: DistanceX(g5) = 16
    c: Angle(g-2,g2) = 1.0472
    c: Symmetric(g1,g5,g-1)
    c: DistanceY(g5,g1) = 200
    c: PointOnObject(g5,g0)
    c: PointOnObject(g5,g1)
    c: Tangent(g0,g4) = -1.5708
    c: Tangent(g1,g4) = -1.5708
    c: Diameter(g4) = 3
FEATURE [PartDesign::Pad] Pad023
  BaseFeature = -> BaseBend003
  Direction = (0,0,1)
  Length = 0.3
  Length2 = 10
  Profile = -> Sketch090
  ReferenceAxis = -> Sketch090 [N_Axis]
  Reversed = true
  Type = 0
FEATURE [PartDesign::Mirrored] Mirrored034
  BaseFeature = -> Pad023
  MirrorPlane = -> Sketch090 [V_Axis]
  Originals = -> [Pad023]
  Refine = true
FEATURE [Sketcher::SketchObject] Sketch091
  FullyConstrained = true
  MapMode = 5
  Placement = pos=(0,0,0) rot=(0.57735,0.57735,0.57735;2.0944rad)
  Support = -> [YZ_Plane029]
  sketch-geometry (8):
    g0: LineSegment StartX=0 StartY=-36.5 StartZ=0 EndX=0 EndY=-18.63 EndZ=0
    g1: LineSegment StartX=0 StartY=-18.63 StartZ=0 EndX=17.4865 EndY=-18.63 EndZ=0
    g2: LineSegment StartX=54.2 StartY=-36.5 StartZ=0 EndX=54.2 EndY=-18.63 EndZ=0
    g3: ArcOfCircle CenterX=36.33 CenterY=-18.63 CenterZ=0 NormalX=0 NormalY=0 NormalZ=1 AngleXU=0 Radius=17.87 StartAngle=4.71239 EndAngle=6.28319
    g4: LineSegment StartX=54.2 StartY=-36.5 StartZ=0 EndX=36.33 EndY=-36.5 EndZ=0
    g5: ArcOfCircle CenterX=36.33 CenterY=-18.63 CenterZ=0 NormalX=0 NormalY=0 NormalZ=1 AngleXU=0 Radius=17.87 StartAngle=3.19461 EndAngle=4.71239
    g6: ArcOfCircle CenterX=17.4865 CenterY=-19.63 CenterZ=0 NormalX=0 NormalY=0 NormalZ=1 AngleXU=0 Radius=1 StartAngle=0.053019 EndAngle=1.5708
    g7: LineSegment StartX=0 StartY=-36.5 StartZ=0 EndX=36.33 EndY=-36.5 EndZ=0
  constraints (22):
    c: PointOnObject(g0,g-2)
    c: PointOnObject(g0,g-2)
    c: Coincident(g0,g1)
    c: Horizontal(g1)
    c: Vertical(g2)
    c: Coincident(g4,g2)
    c: Horizontal(g4)
    c: Tangent(g3,g2) = -1.5708
    c: Coincident(g5,g3)
    c: Coincident(g5,g3)
    c: Tangent(g1,g6) = 1.5708
    c: Tangent(g6,g5) = 1.5708
    c: Coincident(g7,g0)
    c: Coincident(g7,g3)
    c: Horizontal(g7)
    c: Coincident(g3,g4)
    c: Tangent(g5,g7)
    c: DistanceY(g0) = -36.5
    c: DistanceX(g2) = 54.2
    c: Diameter(g6) = 2
    c: Diameter(g5) = 35.74
    c: Horizontal(g0,g2)
FEATURE [PartDesign::Pocket] Pocket050
  BaseFeature = -> Mirrored034
  Direction = (-1,2e-16,-3e-16)
  Length = 5
  Length2 = 5
  Midplane = true
  Profile = -> Sketch091
  ReferenceAxis = -> Sketch091 [N_Axis]
  Refine = true
  Type = 1
FEATURE [PartDesign::Mirrored] Mirrored035
  BaseFeature = -> Pocket050
  MirrorPlane = -> Sketch091 [V_Axis]
  Originals = -> [Pocket050]
FEATURE [Sketcher::SketchObject] Sketch092
  FullyConstrained = true
  MapMode = 5
  Placement = pos=(0,0,0) rot=(0.57735,0.57735,0.57735;2.0944rad)
  Support = -> [YZ_Plane029]
  sketch-geometry (1):
    g0: Circle CenterX=0 CenterY=-9.63 CenterZ=0 NormalX=0 NormalY=0 NormalZ=1 AngleXU=0 Radius=1.65
  constraints (3):
    c: PointOnObject(g0,g-2)
    c: Diameter(g0) = 3.3
    c: DistanceY(g0) = -9.63
FEATURE [PartDesign::Pocket] Pocket051
  BaseFeature = -> Mirrored035
  Direction = (-1,2e-16,-3e-16)
  Length = 5
  Length2 = 5
  Midplane = true
  Profile = -> Sketch092
  ReferenceAxis = -> Sketch092 [N_Axis]
  Type = 1
FEATURE [PartDesign::Body] Body_2  label="top_material_0.50ansi"
  Group = -> [LCS_0,Sketch089,BaseBend003,Sketch090,Pad023,Mirrored034,Sketch091,Pocket050,Mirrored035,Sketch092,Pocket051]
  Origin = -> Origin029
  Placement = pos=(0,0,3) rot=(0,0,1;0rad)
  Tip = -> Pocket051
COMPONENT P15 — recipe-attached ("top_small_material_0.50ansi", modeled in this document).
Construction recipe (the document's own serialized feature program — sketch geometry with constraints, then the solid features built on it; lengths are millimeters unless a unit is written):

FEATURE [PartDesign::CoordinateSystem] LCS_0001
  AttacherType = Attacher::AttachEngine3D
  MapMode = 2
  Support = -> [X_Axis030]
FEATURE [Sketcher::SketchObject] Sketch093  label="Stainless_top_Sketch"
  FullyConstrained = true
  MapMode = 5
  Placement = pos=(0,0,0) rot=(1,0,0;1.5708rad)
  Support = -> [XZ_Plane030]
  sketch-geometry (5):
    g0: LineSegment StartX=-38 StartY=-33.5 StartZ=0 EndX=-38 EndY=0 EndZ=0
    g1: LineSegment StartX=-38 StartY=0 StartZ=0 EndX=38 EndY=0 EndZ=0
    g2: LineSegment StartX=38 StartY=0 StartZ=0 EndX=38 EndY=-33.5 EndZ=0
    g3: LineSegment StartX=38 StartY=-33.5 StartZ=0 EndX=-38 EndY=-33.5 EndZ=0
    g4: GeomPoint X=0 Y=-16.75 Z=0
  constraints (13):
    c: Coincident(g0,g1)
    c: Coincident(g1,g2)
    c: Coincident(g2,g3)
    c: Coincident(g3,g0)
    c: Horizontal(g1)
    c: Horizontal(g3)
    c: Vertical(g0)
    c: Vertical(g2)
    c: Symmetric(g1,g0,g4)
    c: PointOnObject(g4,g-2)
    c: PointOnObject(g1,g-1)
    c: DistanceX(g1,g1) = 76  'width'
    c: DistanceY(g2,g1) = 33.5  'height'
FEATURE [PartDesign::FeaturePython] BaseBend004  # WARN: FeaturePython — macro-defined, semantics opaque (R4)
  BendSide = 0
  BendSketch = -> Sketch093
  MidPlane = true
  Reverse = false
  length = 108.4
  radius = 2
  thickness = 0.5
  expr: length = BaseBend003.length
FEATURE [PartDesign::SubShapeBinder] Binder024
  BindCopyOnChange = 0
  BindMode = 0
  ClaimChildren = false
  Context = -> Body_3 [Binder024.]
  Fuse = false
  MakeFace = true
  OffsetFill = true
  OffsetIntersection = false
  OffsetJoinType = 0
  OffsetOpenResult = true
  PartialLoad = false
  Relative = true
  Support = -> [Body_2[Pocket050.Sketch091.]]
  _Version = 2
FEATURE [PartDesign::Pocket] Pocket052
  BaseFeature = -> BaseBend004
  Direction = (-1,2e-16,-2e-16)
  Length = 5
  Length2 = 5
  Midplane = true
  Profile = -> Binder024 [Face1]
  Type = 1
FEATURE [PartDesign::Mirrored] Mirrored036
  BaseFeature = -> Pocket052
  MirrorPlane = -> XZ_Plane030
  Originals = -> [Pocket052]
FEATURE [PartDesign::SubShapeBinder] Binder025
  BindCopyOnChange = 0
  BindMode = 0
  ClaimChildren = false
  Context = -> Body_3 [Binder025.]
  Fuse = false
  MakeFace = true
  OffsetFill = false
  OffsetIntersection = false
  OffsetJoinType = 0
  OffsetOpenResult = false
  PartialLoad = false
  Relative = true
  Support = -> [Body_2[Pocket051.Sketch092.]]
  _Version = 2
FEATURE [PartDesign::Pocket] Pocket053
  BaseFeature = -> Mirrored036
  Direction = (-1,2e-16,-2e-16)
  Length = 5
  Length2 = 5
  Midplane = true
  Profile = -> Binder025
  Type = 1
FEATURE [PartDesign::SubShapeBinder] Binder031
  BindCopyOnChange = 0
  BindMode = 0
  ClaimChildren = false
  Context = -> Body_3 [Binder031.]
  Fuse = false
  MakeFace = true
  OffsetFill = false
  OffsetIntersection = false
  OffsetJoinType = 0
  OffsetOpenResult = false
  PartialLoad = false
  Relative = true
  _Version = 2
FEATURE [PartDesign::Pocket] Pocket060
  BaseFeature = -> Pocket053
  Direction = (0,0,-1)
  Length = 5
  Length2 = 5
  Midplane = true
  Profile = -> Binder031
  Type = 1
FEATURE [PartDesign::Body] Body_3  label="top_small_material_0.50ansi"
  Group = -> [LCS_0001,Sketch093,BaseBend004,Binder024,Pocket052,Mirrored036,Binder025,Pocket053,Pocket060,Binder031]
  Origin = -> Origin030
  Tip = -> Pocket060
COMPONENT P16 — recipe-attached ("vodostok_s_material_0.30ansi", modeled in this document).
Construction recipe (the document's own serialized feature program — sketch geometry with constraints, then the solid features built on it; lengths are millimeters unless a unit is written):

FEATURE [PartDesign::CoordinateSystem] LCS_0002
  AttacherType = Attacher::AttachEngine3D
  MapMode = 2
  Support = -> [X_Axis032]
FEATURE [Sketcher::SketchObject] Sketch094
  FullyConstrained = true
  MapMode = 5
  Support = -> [XY_Plane033]
  expr: Constraints[5] = <<main>>.rivet_d
  expr: Constraints[6] = <<module>>.module_width + 24mm
  sketch-geometry (3):
    g0: Circle CenterX=-86 CenterY=2e-16 CenterZ=0 NormalX=0 NormalY=0 NormalZ=1 AngleXU=0 Radius=1.7
    g1: Circle CenterX=86 CenterY=0 CenterZ=0 NormalX=0 NormalY=0 NormalZ=1 AngleXU=0 Radius=1.7
    g2: Circle CenterX=86 CenterY=-45 CenterZ=0 NormalX=0 NormalY=0 NormalZ=1 AngleXU=0 Radius=1.7
  constraints (8):
    c: PointOnObject(g1,g-1)
    c: Vertical(g2,g1)
    c: Symmetric(g0,g1,g-2)
    c: Equal(g0,g1)
    c: Equal(g1,g2)
    c: Diameter(g1) = 3.4
    c: DistanceX(g0,g1) = 172
    c: DistanceY(g2,g1) = 45
FEATURE [Sketcher::SketchObject] Sketch095
  FullyConstrained = true
  MapMode = 5
  Support = -> [XY_Plane033]
  expr: Constraints[31] = 10
  expr: Constraints[43] = <<module>>.module_width + 24mm
  expr: Constraints[44] = <<module>>.module_width
  sketch-geometry (31):
    g0: LineSegment StartX=96 StartY=-87.0059 StartZ=0 EndX=96 EndY=5 EndZ=0
    g1: LineSegment StartX=91 StartY=10 StartZ=0 EndX=-91 EndY=10 EndZ=0
    g2: LineSegment StartX=-96 StartY=5 StartZ=0 EndX=-96 EndY=-5 EndZ=0
    g3: LineSegment StartX=-91 StartY=-10 StartZ=0 EndX=-77 EndY=-10 EndZ=0
    g4: LineSegment StartX=-72 StartY=-15 StartZ=0 EndX=-72 EndY=-59.848 EndZ=0
    g5: LineSegment StartX=-48.163 StartY=-99.1271 StartZ=0 EndX=88.7532 EndY=-94.5016 EndZ=0
    g6: ArcOfCircle CenterX=91 CenterY=5 CenterZ=0 NormalX=0 NormalY=0 NormalZ=1 AngleXU=0 Radius=5 StartAngle=0 EndAngle=1.5708
    g7: GeomPoint X=96 Y=10 Z=0
    g8: ArcOfCircle CenterX=-91 CenterY=-5 CenterZ=0 NormalX=0 NormalY=0 NormalZ=1 AngleXU=0 Radius=5 StartAngle=3.14159 EndAngle=4.71239
    g9: GeomPoint X=-96 Y=-10 Z=0
    g10: ArcOfCircle CenterX=-91 CenterY=5 CenterZ=0 NormalX=0 NormalY=0 NormalZ=1 AngleXU=0 Radius=5 StartAngle=1.5708 EndAngle=3.14159
    g11: GeomPoint X=-96 Y=10 Z=0
    g12: ArcOfCircle CenterX=-77 CenterY=-15 CenterZ=0 NormalX=0 NormalY=0 NormalZ=1 AngleXU=0 Radius=5 StartAngle=0 EndAngle=1.5708
    g13: GeomPoint X=-72 Y=-10 Z=0
    g14: GeomPoint X=-72 Y=-99.9324 Z=0
    g15: ArcOfCircle CenterX=88.5 CenterY=-87.0059 CenterZ=0 NormalX=0 NormalY=0 NormalZ=1 AngleXU=0 Radius=7.5 StartAngle=4.74616 EndAngle=6.28319
    g16: GeomPoint X=96 Y=-94.2568 Z=0
    g17: LineSegment StartX=-72 StartY=-59.9324 StartZ=0 EndX=96 EndY=-54.2568 EndZ=0
    g18: LineSegment StartX=-91 StartY=5 StartZ=0 EndX=-91 EndY=0 EndZ=0
    g19: LineSegment StartX=-91 StartY=0 StartZ=0 EndX=-91 EndY=-5 EndZ=0
    g20: GeomPoint X=86 Y=0 Z=0
    g21: GeomPoint X=-86 Y=0 Z=0
    g22: GeomPoint X=74 Y=0 Z=0
    g23: GeomPoint X=-74 Y=0 Z=0
    g24: LineSegment StartX=-91 StartY=-5 StartZ=0 EndX=-86 EndY=0 EndZ=0
    g25: GeomPoint X=-74 Y=-60 Z=0
    g26: GeomPoint X=74 Y=-55 Z=0
    g27: LineSegment StartX=-71.9971 StartY=-60.0168 StartZ=0 EndX=-71.4099 EndY=-77.3997 EndZ=0
    g28: ArcOfCircle CenterX=-48.9227 CenterY=-76.64 CenterZ=0 NormalX=0 NormalY=0 NormalZ=1 AngleXU=0 Radius=22.5 StartAngle=3.17536 EndAngle=4.74616
    g29: ArcOfCircle CenterX=-67 CenterY=-59.848 CenterZ=0 NormalX=0 NormalY=0 NormalZ=1 AngleXU=0 Radius=5 StartAngle=3.14159 EndAngle=3.17536
    g30: GeomPoint X=-72 Y=-59.9324 Z=0
  constraints (69):
    c: Vertical(g0)
    c: Horizontal(g1)
    c: Vertical(g2)
    c: Horizontal(g3)
    c: Vertical(g4)
    c: PointOnObject(g7,g1)
    c: PointOnObject(g7,g0)
    c: Tangent(g1,g6) = -1.5708
    c: Tangent(g0,g6) = -1.5708
    c: PointOnObject(g9,g3)
    c: PointOnObject(g9,g2)
    c: Tangent(g3,g8) = -1.5708
    c: Tangent(g2,g8) = -1.5708
    c: PointOnObject(g11,g2)
    c: PointOnObject(g11,g1)
    c: Tangent(g2,g10) = -1.5708
    c: Tangent(g1,g10) = -1.5708
    c: PointOnObject(g13,g3)
    c: PointOnObject(g13,g4)
    c: Tangent(g3,g12) = 1.5708
    c: Tangent(g4,g12) = 1.5708
    c: PointOnObject(g14,g4)
    c: PointOnObject(g14,g5)
    c: PointOnObject(g16,g5)
    c: PointOnObject(g16,g0)
    c: Tangent(g5,g15) = -1.5708
    c: Tangent(g0,g15) = -1.5708
    c: Parallel(g17,g5)
    c: Equal(g12,g8)
    c: Equal(g8,g10)
    c: Equal(g10,g6)
    c: Diameter(g10) = 10
    c: Diameter(g15) = 15
    c: Coincident(g18,g10)
    c: PointOnObject(g18,g-1)
    c: Vertical(g18)
    c: Coincident(g18,g19)
    c: Coincident(g19,g8)
    c: Equal(g19,g18)
    c: PointOnObject(g20,g-1)
    c: PointOnObject(g22,g-1)
    c: Symmetric(g21,g20,g-2)
    c: Symmetric(g23,g22,g-2)
    c: DistanceX(g21,g20) = 172
    c: DistanceX(g23,g22) = 148
    c: DistanceY(g9,g11) = 20
    c: Coincident(g24,g8)
    c: Coincident(g24,g21)
    c: Angle(g24,g-1) = 2.35619
    c: DistanceY(g16,g17) = 40
    c: DistanceX(g22,g0) = 22
    c: Vertical(g22,g26)
    c: Vertical(g25,g23)
    c: DistanceY(g25,g26) = 5
    c: PointOnObject(g26,g17)
    c: PointOnObject(g25,g17)
    c: DistanceY(g26,g22) = 55
    c: Coincident(g30,g17)
    c: Perpendicular(g27,g17)
    c: Tangent(g28,g5) = -1.5708
    c: Tangent(g28,g27) = -1.5708
    c: PointOnObject(g17,g0)
    c: Diameter(g28) = 45
    c: DistanceX(g23,g13) = 2
    c: PointOnObject(g30,g27)
    c: PointOnObject(g30,g4)
    c: Tangent(g27,g29) = -1.5708
    c: Tangent(g4,g29) = -1.5708
    c: Diameter(g29) = 10
FEATURE [PartDesign::Pad] Pad025
  Direction = (0,0,1)
  Length = 0.5
  Length2 = 10
  Profile = -> Sketch095
  ReferenceAxis = -> Sketch095 [N_Axis]
  Type = 0
FEATURE [Sketcher::SketchObject] Sketch096
  AttachmentOffset = pos=(0,0,0.5) rot=(0,0,1;0rad)
  FullyConstrained = false
  MapMode = 5
  Placement = pos=(0,0,0.5) rot=(0,0,1;0rad)
  Support = -> [XY_Plane033]
  expr: .AttachmentOffset.Base.z = Pad025.Length
  expr: Constraints[4] = <<module>>.module_width
  sketch-geometry (5):
    g0: GeomPoint X=-74 Y=0 Z=0
    g1: GeomPoint X=74 Y=0 Z=0
    g2: GeomPoint X=74 Y=-58 Z=0
    g3: GeomPoint X=-74 Y=-63 Z=0
    g4: LineSegment StartX=-105.813 StartY=-64.0748 StartZ=0 EndX=129.863 EndY=-56.1127 EndZ=0
  constraints (9):
    c: PointOnObject(g1,g-1)
    c: DistanceY(g3,g2) = 5
    c: DistanceY(g2,g1) = 58
    c: Symmetric(g0,g1,g-1)
    c: DistanceX(g0,g1) = 148
    c: Vertical(g2,g1)
    c: Vertical(g3,g0)
    c: PointOnObject(g2,g4)
    c: PointOnObject(g3,g4)
FEATURE [Sketcher::SketchObject] Sketch097
  FullyConstrained = false
  MapMode = 5
  Support = -> [XY_Plane033]
  sketch-geometry (1):
    g0: Circle CenterX=-66 CenterY=-66.2266 CenterZ=0 NormalX=0 NormalY=0 NormalZ=1 AngleXU=0 Radius=2.5
  constraints (2):
    c: Diameter(g0) = 5
    c: DistanceX(g0) = -66
FEATURE [PartDesign::Pocket] Pocket054
  BaseFeature = -> Pad025
  Direction = (0,0,-1)
  Length = 5
  Length2 = 5
  Midplane = true
  Profile = -> Sketch097
  ReferenceAxis = -> Sketch097 [N_Axis]
  Type = 1
FEATURE [PartDesign::Pocket] Pocket055
  BaseFeature = -> Pocket054
  Direction = (0,0,-1)
  Length = 5
  Length2 = 5
  Midplane = true
  Profile = -> Sketch094
  ReferenceAxis = -> Sketch094 [N_Axis]
  Type = 1
FEATURE [PartDesign::FeaturePython] Fold009  # WARN: FeaturePython — macro-defined, semantics opaque (R4)
  BaseFeature = -> Pocket055
  BendLine = -> Sketch096
  Position = 0
  angle = 105
  baseObject = -> Pocket055 [Face5]
  invert = false
  invertbend = false
  kfactor = 0.5
  radius = 2
  unfold = false
FEATURE [PartDesign::Body] Body_4  label="vodostok_s_material_0.30ansi"
  Group = -> [LCS_0002,Sketch094,Sketch095,Pad025,Sketch096,Sketch097,Pocket054,Pocket055,Fold009]
  Origin = -> Origin032
  Tip = -> Fold009
